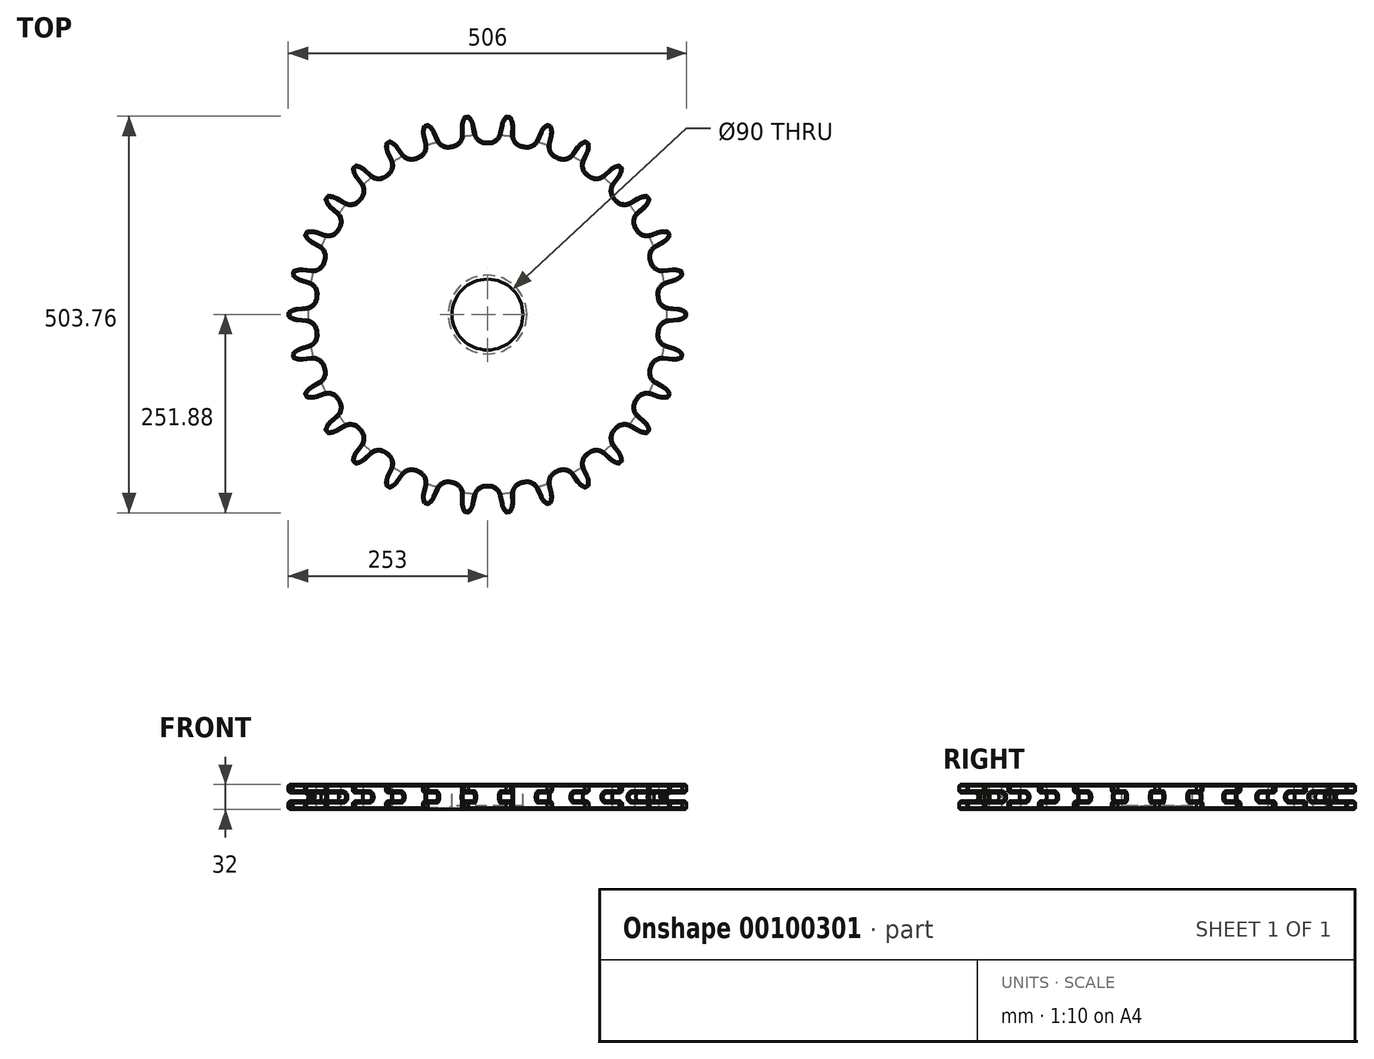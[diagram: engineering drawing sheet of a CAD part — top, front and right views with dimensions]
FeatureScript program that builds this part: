
annotation { "Feature Type Name" : "Feature", "Feature Type Description" : "" }
export const myFeature = defineFeature(function(context is Context, id is Id, definition is map)
    precondition{}
    {
        {
            var Q0;
            Q0=qCreatedBy(makeId("Top.planeOp"),FACE);
            var sketch = newSketch(context, id + "F0", { "sketchPlane" : qUnion([Q0])});
            skCircle(sketch, "E0", {"center": v(0, 0) * mm, "radius": 253 * mm});
            skCircle(sketch, "E1", {"center": v(0, 0) * mm, "radius": 216.9 * mm, "construction": true});
            skLineSegment(sketch, "E2", {"start": v(0, 0) * mm, "end": v(253, 0) * mm, "construction": true});
            skLineSegment(sketch, "E3", {"start": v(0, 0) * mm, "end": v(252.65, -13.34) * mm, "construction": true});
            skCircle(sketch, "E4", {"center": v(0, 0) * mm, "radius": 239.77 * mm, "construction": true});
            skCircle(sketch, "E5", {"center": v(239.43, -12.64) * mm, "radius": 20.44 * mm});
            skLineSegment(sketch, "E6", {"start": v(0, 0) * mm, "end": v(251.8, 24.61) * mm, "construction": true});
            skCircle(sketch, "E7", {"center": v(0, 0) * mm, "radius": 232.9 * mm, "construction": true});
            skCircle(sketch, "E8", {"center": v(231.8, 22.66) * mm, "radius": 14 * mm});
            skLineSegment(sketch, "E9", {"start": v(230.5, 8.72) * mm, "end": v(241.32, 7.72) * mm});
            skCircle(sketch, "E10", {"center": v(0, 0) * mm, "radius": 218.9 * mm});
            skSolve(sketch);
        }
        {
            var Q0;
            Q0=qCreatedBy(makeId("Top.planeOp"),FACE);
            var sketch = newSketch(context, id + "F1", { "sketchPlane" : qUnion([Q0])});
            skArc(sketch, "E11.0", {"start": v(217.86, 21.3) * mm, "mid": v(221.92, 12.73) * mm, "end": v(230.5, 8.72) * mm});
            skArc(sketch, "E12.0", {"start": v(252.99, 2.67) * mm, "mid": v(247.56, 6.12) * mm, "end": v(241.32, 7.72) * mm});
            skArc(sketch, "E13.0", {"start": v(253, 0) * mm, "mid": v(253, 1.33) * mm, "end": v(252.99, 2.67) * mm});
            skLineSegment(sketch, "E14.0", {"start": v(0, 0) * mm, "end": v(253, 0) * mm, "construction": true});
            skLineSegment(sketch, "E15.0", {"start": v(230.5, 8.72) * mm, "end": v(241.32, 7.72) * mm});
            skArc(sketch, "E16.MirrorCS", {"start": v(253, 0) * mm, "mid": v(253, -1.33) * mm, "end": v(252.99, -2.67) * mm});
            skArc(sketch, "E17.MirrorCS", {"start": v(252.99, -2.67) * mm, "mid": v(247.56, -6.12) * mm, "end": v(241.32, -7.72) * mm});
            skLineSegment(sketch, "E18.MirrorCS", {"start": v(230.5, -8.72) * mm, "end": v(241.32, -7.72) * mm});
            skArc(sketch, "E19.MirrorCS", {"start": v(217.86, -21.3) * mm, "mid": v(221.92, -12.73) * mm, "end": v(230.5, -8.72) * mm});
            skLineSegment(sketch, "E20.1.0", {"start": v(0, 0) * mm, "end": v(247.47, 52.6) * mm, "construction": true});
            skArc(sketch, "E20.1.1", {"start": v(208.68, 66.13) * mm, "mid": v(214.43, 58.6) * mm, "end": v(223.66, 56.45) * mm});
            skLineSegment(sketch, "E20.1.2", {"start": v(223.66, 56.45) * mm, "end": v(234.44, 57.72) * mm});
            skArc(sketch, "E20.1.3", {"start": v(246.9, 55.2) * mm, "mid": v(240.87, 57.46) * mm, "end": v(234.44, 57.72) * mm});
            skArc(sketch, "E20.1.4", {"start": v(247.47, 52.6) * mm, "mid": v(247.2, 53.9) * mm, "end": v(246.9, 55.2) * mm});
            skArc(sketch, "E20.1.5", {"start": v(247.47, 52.6) * mm, "mid": v(247.75, 51.3) * mm, "end": v(248.01, 50) * mm});
            skArc(sketch, "E20.1.6", {"start": v(248.01, 50) * mm, "mid": v(243.42, 45.48) * mm, "end": v(237.65, 42.63) * mm});
            skLineSegment(sketch, "E20.1.7", {"start": v(227.28, 39.4) * mm, "end": v(237.65, 42.63) * mm});
            skArc(sketch, "E20.1.8", {"start": v(217.53, 24.47) * mm, "mid": v(219.72, 33.68) * mm, "end": v(227.28, 39.4) * mm});
            skLineSegment(sketch, "E20.2.0", {"start": v(0, 0) * mm, "end": v(231.13, 102.9) * mm, "construction": true});
            skArc(sketch, "E20.2.1", {"start": v(190.37, 108.07) * mm, "mid": v(197.56, 101.9) * mm, "end": v(207.03, 101.72) * mm});
            skLineSegment(sketch, "E20.2.2", {"start": v(207.03, 101.72) * mm, "end": v(217.32, 105.2) * mm});
            skArc(sketch, "E20.2.3", {"start": v(230.03, 105.33) * mm, "mid": v(223.66, 106.28) * mm, "end": v(217.32, 105.2) * mm});
            skArc(sketch, "E20.2.4", {"start": v(231.13, 102.9) * mm, "mid": v(230.58, 104.12) * mm, "end": v(230.03, 105.33) * mm});
            skArc(sketch, "E20.2.5", {"start": v(231.13, 102.9) * mm, "mid": v(231.67, 101.69) * mm, "end": v(232.2, 100.46) * mm});
            skArc(sketch, "E20.2.6", {"start": v(232.2, 100.46) * mm, "mid": v(228.64, 95.1) * mm, "end": v(223.6, 91.1) * mm});
            skLineSegment(sketch, "E20.2.7", {"start": v(214.12, 85.8) * mm, "end": v(223.6, 91.1) * mm});
            skArc(sketch, "E20.2.8", {"start": v(207.7, 69.16) * mm, "mid": v(207.92, 78.63) * mm, "end": v(214.12, 85.8) * mm});
            skLineSegment(sketch, "E21.1.3.0", {"start": v(0, 0) * mm, "end": v(204.68, 148.7) * mm, "construction": true});
            skArc(sketch, "E21.3.3.0", {"start": v(163.74, 145.29) * mm, "mid": v(172.06, 140.75) * mm, "end": v(181.36, 142.54) * mm});
            skLineSegment(sketch, "E21.7.3.0", {"start": v(181.36, 142.54) * mm, "end": v(190.7, 148.09) * mm});
            skArc(sketch, "E21.10.3.0", {"start": v(203.1, 150.86) * mm, "mid": v(196.68, 150.46) * mm, "end": v(190.7, 148.09) * mm});
            skArc(sketch, "E21.14.3.0", {"start": v(204.68, 148.7) * mm, "mid": v(203.9, 149.79) * mm, "end": v(203.1, 150.86) * mm});
            skArc(sketch, "E21.18.3.0", {"start": v(204.68, 148.7) * mm, "mid": v(205.46, 147.63) * mm, "end": v(206.24, 146.54) * mm});
            skArc(sketch, "E21.22.3.0", {"start": v(206.24, 146.54) * mm, "mid": v(203.87, 140.56) * mm, "end": v(199.77, 135.6) * mm});
            skLineSegment(sketch, "E21.26.3.0", {"start": v(191.6, 128.44) * mm, "end": v(199.77, 135.6) * mm});
            skArc(sketch, "E21.29.3.0", {"start": v(188.77, 110.83) * mm, "mid": v(187.02, 120.14) * mm, "end": v(191.6, 128.44) * mm});
            skLineSegment(sketch, "E21.1.4.0", {"start": v(0, 0) * mm, "end": v(169.3, 188.02) * mm, "construction": true});
            skArc(sketch, "E21.3.4.0", {"start": v(129.95, 176.16) * mm, "mid": v(139.03, 173.44) * mm, "end": v(147.76, 177.13) * mm});
            skLineSegment(sketch, "E21.7.4.0", {"start": v(147.76, 177.13) * mm, "end": v(155.74, 184.5) * mm});
            skArc(sketch, "E21.10.4.0", {"start": v(167.3, 189.79) * mm, "mid": v(161.1, 188.07) * mm, "end": v(155.74, 184.5) * mm});
            skArc(sketch, "E21.14.4.0", {"start": v(169.3, 188.02) * mm, "mid": v(168.3, 188.9) * mm, "end": v(167.3, 189.79) * mm});
            skArc(sketch, "E21.18.4.0", {"start": v(169.3, 188.02) * mm, "mid": v(170.28, 187.12) * mm, "end": v(171.26, 186.22) * mm});
            skArc(sketch, "E21.22.4.0", {"start": v(171.26, 186.22) * mm, "mid": v(170.2, 179.87) * mm, "end": v(167.2, 174.17) * mm});
            skLineSegment(sketch, "E21.26.4.0", {"start": v(160.72, 165.47) * mm, "end": v(167.2, 174.17) * mm});
            skArc(sketch, "E21.29.4.0", {"start": v(161.6, 147.65) * mm, "mid": v(157.96, 156.4) * mm, "end": v(160.72, 165.47) * mm});
            skLineSegment(sketch, "E21.1.5.0", {"start": v(0, 0) * mm, "end": v(126.5, 219.1) * mm, "construction": true});
            skArc(sketch, "E21.3.5.0", {"start": v(90.49, 199.32) * mm, "mid": v(99.93, 198.56) * mm, "end": v(107.7, 203.98) * mm});
            skLineSegment(sketch, "E21.7.5.0", {"start": v(107.7, 203.98) * mm, "end": v(113.98, 212.85) * mm});
            skArc(sketch, "E21.10.5.0", {"start": v(124.18, 220.43) * mm, "mid": v(118.48, 217.45) * mm, "end": v(113.98, 212.85) * mm});
            skArc(sketch, "E21.14.5.0", {"start": v(126.5, 219.1) * mm, "mid": v(125.34, 219.77) * mm, "end": v(124.18, 220.43) * mm});
            skArc(sketch, "E21.18.5.0", {"start": v(126.5, 219.1) * mm, "mid": v(127.65, 218.43) * mm, "end": v(128.8, 217.76) * mm});
            skArc(sketch, "E21.22.5.0", {"start": v(128.8, 217.76) * mm, "mid": v(129.08, 211.33) * mm, "end": v(127.34, 205.13) * mm});
            skLineSegment(sketch, "E21.26.5.0", {"start": v(122.8, 195.27) * mm, "end": v(127.34, 205.13) * mm});
            skArc(sketch, "E21.29.5.0", {"start": v(127.38, 178.03) * mm, "mid": v(121.99, 185.82) * mm, "end": v(122.8, 195.27) * mm});
            skLineSegment(sketch, "E22.1.6.0", {"start": v(0, 0) * mm, "end": v(78.18, 240.62) * mm, "construction": true});
            skArc(sketch, "E22.3.6.0", {"start": v(47.07, 213.78) * mm, "mid": v(56.47, 215) * mm, "end": v(62.94, 221.92) * mm});
            skLineSegment(sketch, "E22.7.6.0", {"start": v(62.94, 221.92) * mm, "end": v(67.23, 231.9) * mm});
            skArc(sketch, "E22.10.6.0", {"start": v(75.64, 241.43) * mm, "mid": v(70.68, 237.33) * mm, "end": v(67.23, 231.9) * mm});
            skArc(sketch, "E22.14.6.0", {"start": v(78.18, 240.62) * mm, "mid": v(76.91, 241.03) * mm, "end": v(75.64, 241.43) * mm});
            skArc(sketch, "E22.18.6.0", {"start": v(78.18, 240.62) * mm, "mid": v(79.45, 240.2) * mm, "end": v(80.71, 239.78) * mm});
            skArc(sketch, "E22.22.6.0", {"start": v(80.71, 239.78) * mm, "mid": v(82.32, 233.55) * mm, "end": v(81.91, 227.12) * mm});
            skLineSegment(sketch, "E22.26.6.0", {"start": v(79.52, 216.53) * mm, "end": v(81.91, 227.12) * mm});
            skArc(sketch, "E22.29.6.0", {"start": v(87.58, 200.62) * mm, "mid": v(80.69, 207.13) * mm, "end": v(79.52, 216.53) * mm});
            skLineSegment(sketch, "E22.1.7.0", {"start": v(0, 0) * mm, "end": v(26.45, 251.61) * mm, "construction": true});
            skArc(sketch, "E22.3.7.0", {"start": v(1.6, 218.9) * mm, "mid": v(10.53, 222.04) * mm, "end": v(15.42, 230.16) * mm});
            skLineSegment(sketch, "E22.7.7.0", {"start": v(15.42, 230.16) * mm, "end": v(17.55, 240.8) * mm});
            skArc(sketch, "E22.10.7.0", {"start": v(23.8, 251.88) * mm, "mid": v(19.79, 246.84) * mm, "end": v(17.55, 240.8) * mm});
            skArc(sketch, "E22.14.7.0", {"start": v(26.45, 251.61) * mm, "mid": v(25.12, 251.75) * mm, "end": v(23.8, 251.88) * mm});
            skArc(sketch, "E22.18.7.0", {"start": v(26.45, 251.61) * mm, "mid": v(27.77, 251.47) * mm, "end": v(29.1, 251.32) * mm});
            skArc(sketch, "E22.22.7.0", {"start": v(29.1, 251.32) * mm, "mid": v(31.96, 245.56) * mm, "end": v(32.9, 239.2) * mm});
            skLineSegment(sketch, "E22.26.7.0", {"start": v(32.77, 228.33) * mm, "end": v(32.9, 239.2) * mm});
            skArc(sketch, "E22.29.7.0", {"start": v(43.95, 214.45) * mm, "mid": v(35.86, 219.38) * mm, "end": v(32.77, 228.33) * mm});
            skLineSegment(sketch, "E22.1.8.0", {"start": v(0, 0) * mm, "end": v(-26.45, 251.61) * mm, "construction": true});
            skArc(sketch, "E22.3.8.0", {"start": v(-43.95, 214.45) * mm, "mid": v(-35.86, 219.38) * mm, "end": v(-32.77, 228.33) * mm});
            skLineSegment(sketch, "E22.7.8.0", {"start": v(-32.77, 228.33) * mm, "end": v(-32.9, 239.2) * mm});
            skArc(sketch, "E22.10.8.0", {"start": v(-29.1, 251.32) * mm, "mid": v(-31.96, 245.56) * mm, "end": v(-32.9, 239.2) * mm});
            skArc(sketch, "E22.14.8.0", {"start": v(-26.45, 251.61) * mm, "mid": v(-27.77, 251.47) * mm, "end": v(-29.1, 251.32) * mm});
            skArc(sketch, "E22.18.8.0", {"start": v(-26.45, 251.61) * mm, "mid": v(-25.12, 251.75) * mm, "end": v(-23.8, 251.88) * mm});
            skArc(sketch, "E22.22.8.0", {"start": v(-23.8, 251.88) * mm, "mid": v(-19.79, 246.84) * mm, "end": v(-17.55, 240.8) * mm});
            skLineSegment(sketch, "E22.26.8.0", {"start": v(-15.42, 230.16) * mm, "end": v(-17.55, 240.8) * mm});
            skArc(sketch, "E22.29.8.0", {"start": v(-1.6, 218.9) * mm, "mid": v(-10.53, 222.04) * mm, "end": v(-15.42, 230.16) * mm});
            skLineSegment(sketch, "E22.1.9.0", {"start": v(0, 0) * mm, "end": v(-78.18, 240.62) * mm, "construction": true});
            skArc(sketch, "E22.3.9.0", {"start": v(-87.58, 200.62) * mm, "mid": v(-80.69, 207.13) * mm, "end": v(-79.52, 216.53) * mm});
            skLineSegment(sketch, "E22.7.9.0", {"start": v(-79.52, 216.53) * mm, "end": v(-81.91, 227.12) * mm});
            skArc(sketch, "E22.10.9.0", {"start": v(-80.71, 239.78) * mm, "mid": v(-82.32, 233.55) * mm, "end": v(-81.91, 227.12) * mm});
            skArc(sketch, "E22.14.9.0", {"start": v(-78.18, 240.62) * mm, "mid": v(-79.45, 240.2) * mm, "end": v(-80.71, 239.78) * mm});
            skArc(sketch, "E22.18.9.0", {"start": v(-78.18, 240.62) * mm, "mid": v(-76.91, 241.03) * mm, "end": v(-75.64, 241.43) * mm});
            skArc(sketch, "E22.22.9.0", {"start": v(-75.64, 241.43) * mm, "mid": v(-70.68, 237.33) * mm, "end": v(-67.23, 231.9) * mm});
            skLineSegment(sketch, "E22.26.9.0", {"start": v(-62.94, 221.92) * mm, "end": v(-67.23, 231.9) * mm});
            skArc(sketch, "E22.29.9.0", {"start": v(-47.07, 213.78) * mm, "mid": v(-56.47, 215) * mm, "end": v(-62.94, 221.92) * mm});
            skLineSegment(sketch, "E22.1.10.0", {"start": v(0, 0) * mm, "end": v(-126.5, 219.1) * mm, "construction": true});
            skArc(sketch, "E22.3.10.0", {"start": v(-127.38, 178.03) * mm, "mid": v(-121.99, 185.82) * mm, "end": v(-122.8, 195.27) * mm});
            skLineSegment(sketch, "E22.7.10.0", {"start": v(-122.8, 195.27) * mm, "end": v(-127.34, 205.13) * mm});
            skArc(sketch, "E22.10.10.0", {"start": v(-128.8, 217.76) * mm, "mid": v(-129.08, 211.33) * mm, "end": v(-127.34, 205.13) * mm});
            skArc(sketch, "E22.14.10.0", {"start": v(-126.5, 219.1) * mm, "mid": v(-127.65, 218.43) * mm, "end": v(-128.8, 217.76) * mm});
            skArc(sketch, "E22.18.10.0", {"start": v(-126.5, 219.1) * mm, "mid": v(-125.34, 219.77) * mm, "end": v(-124.18, 220.43) * mm});
            skArc(sketch, "E22.22.10.0", {"start": v(-124.18, 220.43) * mm, "mid": v(-118.48, 217.45) * mm, "end": v(-113.98, 212.85) * mm});
            skLineSegment(sketch, "E22.26.10.0", {"start": v(-107.7, 203.98) * mm, "end": v(-113.98, 212.85) * mm});
            skArc(sketch, "E22.29.10.0", {"start": v(-90.49, 199.32) * mm, "mid": v(-99.93, 198.56) * mm, "end": v(-107.7, 203.98) * mm});
            skLineSegment(sketch, "E22.1.11.0", {"start": v(0, 0) * mm, "end": v(-169.3, 188.02) * mm, "construction": true});
            skArc(sketch, "E22.3.11.0", {"start": v(-161.6, 147.65) * mm, "mid": v(-157.96, 156.4) * mm, "end": v(-160.72, 165.47) * mm});
            skLineSegment(sketch, "E22.7.11.0", {"start": v(-160.72, 165.47) * mm, "end": v(-167.2, 174.17) * mm});
            skArc(sketch, "E22.10.11.0", {"start": v(-171.26, 186.22) * mm, "mid": v(-170.2, 179.87) * mm, "end": v(-167.2, 174.17) * mm});
            skArc(sketch, "E22.14.11.0", {"start": v(-169.3, 188.02) * mm, "mid": v(-170.28, 187.12) * mm, "end": v(-171.26, 186.22) * mm});
            skArc(sketch, "E22.18.11.0", {"start": v(-169.3, 188.02) * mm, "mid": v(-168.3, 188.9) * mm, "end": v(-167.3, 189.79) * mm});
            skArc(sketch, "E22.22.11.0", {"start": v(-167.3, 189.79) * mm, "mid": v(-161.1, 188.07) * mm, "end": v(-155.74, 184.5) * mm});
            skLineSegment(sketch, "E22.26.11.0", {"start": v(-147.76, 177.13) * mm, "end": v(-155.74, 184.5) * mm});
            skArc(sketch, "E22.29.11.0", {"start": v(-129.95, 176.16) * mm, "mid": v(-139.03, 173.44) * mm, "end": v(-147.76, 177.13) * mm});
            skLineSegment(sketch, "E22.1.12.0", {"start": v(0, 0) * mm, "end": v(-204.68, 148.7) * mm, "construction": true});
            skArc(sketch, "E22.3.12.0", {"start": v(-188.77, 110.83) * mm, "mid": v(-187.02, 120.14) * mm, "end": v(-191.6, 128.44) * mm});
            skLineSegment(sketch, "E22.7.12.0", {"start": v(-191.6, 128.44) * mm, "end": v(-199.77, 135.6) * mm});
            skArc(sketch, "E22.10.12.0", {"start": v(-206.24, 146.54) * mm, "mid": v(-203.87, 140.56) * mm, "end": v(-199.77, 135.6) * mm});
            skArc(sketch, "E22.14.12.0", {"start": v(-204.68, 148.7) * mm, "mid": v(-205.46, 147.63) * mm, "end": v(-206.24, 146.54) * mm});
            skArc(sketch, "E22.18.12.0", {"start": v(-204.68, 148.7) * mm, "mid": v(-203.9, 149.79) * mm, "end": v(-203.1, 150.86) * mm});
            skArc(sketch, "E22.22.12.0", {"start": v(-203.1, 150.86) * mm, "mid": v(-196.68, 150.46) * mm, "end": v(-190.7, 148.09) * mm});
            skLineSegment(sketch, "E22.26.12.0", {"start": v(-181.36, 142.54) * mm, "end": v(-190.7, 148.09) * mm});
            skArc(sketch, "E22.29.12.0", {"start": v(-163.74, 145.29) * mm, "mid": v(-172.06, 140.75) * mm, "end": v(-181.36, 142.54) * mm});
            skLineSegment(sketch, "E22.1.13.0", {"start": v(0, 0) * mm, "end": v(-231.13, 102.9) * mm, "construction": true});
            skArc(sketch, "E22.3.13.0", {"start": v(-207.7, 69.16) * mm, "mid": v(-207.92, 78.63) * mm, "end": v(-214.12, 85.8) * mm});
            skLineSegment(sketch, "E22.7.13.0", {"start": v(-214.12, 85.8) * mm, "end": v(-223.6, 91.1) * mm});
            skArc(sketch, "E22.10.13.0", {"start": v(-232.2, 100.46) * mm, "mid": v(-228.64, 95.1) * mm, "end": v(-223.6, 91.1) * mm});
            skArc(sketch, "E22.14.13.0", {"start": v(-231.13, 102.9) * mm, "mid": v(-231.67, 101.69) * mm, "end": v(-232.2, 100.46) * mm});
            skArc(sketch, "E22.18.13.0", {"start": v(-231.13, 102.9) * mm, "mid": v(-230.58, 104.12) * mm, "end": v(-230.03, 105.33) * mm});
            skArc(sketch, "E22.22.13.0", {"start": v(-230.03, 105.33) * mm, "mid": v(-223.66, 106.28) * mm, "end": v(-217.32, 105.2) * mm});
            skLineSegment(sketch, "E22.26.13.0", {"start": v(-207.03, 101.72) * mm, "end": v(-217.32, 105.2) * mm});
            skArc(sketch, "E22.29.13.0", {"start": v(-190.37, 108.07) * mm, "mid": v(-197.56, 101.9) * mm, "end": v(-207.03, 101.72) * mm});
            skLineSegment(sketch, "E22.1.14.0", {"start": v(0, 0) * mm, "end": v(-247.47, 52.6) * mm, "construction": true});
            skArc(sketch, "E22.3.14.0", {"start": v(-217.53, 24.47) * mm, "mid": v(-219.72, 33.68) * mm, "end": v(-227.28, 39.4) * mm});
            skLineSegment(sketch, "E22.7.14.0", {"start": v(-227.28, 39.4) * mm, "end": v(-237.65, 42.63) * mm});
            skArc(sketch, "E22.10.14.0", {"start": v(-248.01, 50) * mm, "mid": v(-243.42, 45.48) * mm, "end": v(-237.65, 42.63) * mm});
            skArc(sketch, "E22.14.14.0", {"start": v(-247.47, 52.6) * mm, "mid": v(-247.75, 51.3) * mm, "end": v(-248.01, 50) * mm});
            skArc(sketch, "E22.18.14.0", {"start": v(-247.47, 52.6) * mm, "mid": v(-247.2, 53.9) * mm, "end": v(-246.9, 55.2) * mm});
            skArc(sketch, "E22.22.14.0", {"start": v(-246.9, 55.2) * mm, "mid": v(-240.87, 57.46) * mm, "end": v(-234.44, 57.72) * mm});
            skLineSegment(sketch, "E22.26.14.0", {"start": v(-223.66, 56.45) * mm, "end": v(-234.44, 57.72) * mm});
            skArc(sketch, "E22.29.14.0", {"start": v(-208.68, 66.13) * mm, "mid": v(-214.43, 58.6) * mm, "end": v(-223.66, 56.45) * mm});
            skLineSegment(sketch, "E22.1.15.0", {"start": v(0, 0) * mm, "end": v(-253, 0) * mm, "construction": true});
            skArc(sketch, "E22.3.15.0", {"start": v(-217.86, -21.3) * mm, "mid": v(-221.92, -12.73) * mm, "end": v(-230.5, -8.72) * mm});
            skLineSegment(sketch, "E22.7.15.0", {"start": v(-230.5, -8.72) * mm, "end": v(-241.32, -7.72) * mm});
            skArc(sketch, "E22.10.15.0", {"start": v(-252.99, -2.67) * mm, "mid": v(-247.56, -6.12) * mm, "end": v(-241.32, -7.72) * mm});
            skArc(sketch, "E22.14.15.0", {"start": v(-253, 0) * mm, "mid": v(-253, -1.33) * mm, "end": v(-252.99, -2.67) * mm});
            skArc(sketch, "E22.18.15.0", {"start": v(-253, 0) * mm, "mid": v(-253, 1.33) * mm, "end": v(-252.99, 2.67) * mm});
            skArc(sketch, "E22.22.15.0", {"start": v(-252.99, 2.67) * mm, "mid": v(-247.56, 6.12) * mm, "end": v(-241.32, 7.72) * mm});
            skLineSegment(sketch, "E22.26.15.0", {"start": v(-230.5, 8.72) * mm, "end": v(-241.32, 7.72) * mm});
            skArc(sketch, "E22.29.15.0", {"start": v(-217.86, 21.3) * mm, "mid": v(-221.92, 12.73) * mm, "end": v(-230.5, 8.72) * mm});
            skLineSegment(sketch, "E22.1.16.0", {"start": v(0, 0) * mm, "end": v(-247.47, -52.6) * mm, "construction": true});
            skArc(sketch, "E22.3.16.0", {"start": v(-208.68, -66.13) * mm, "mid": v(-214.43, -58.6) * mm, "end": v(-223.66, -56.45) * mm});
            skLineSegment(sketch, "E22.7.16.0", {"start": v(-223.66, -56.45) * mm, "end": v(-234.44, -57.72) * mm});
            skArc(sketch, "E22.10.16.0", {"start": v(-246.9, -55.2) * mm, "mid": v(-240.87, -57.46) * mm, "end": v(-234.44, -57.72) * mm});
            skArc(sketch, "E22.14.16.0", {"start": v(-247.47, -52.6) * mm, "mid": v(-247.2, -53.9) * mm, "end": v(-246.9, -55.2) * mm});
            skArc(sketch, "E22.18.16.0", {"start": v(-247.47, -52.6) * mm, "mid": v(-247.75, -51.3) * mm, "end": v(-248.01, -50) * mm});
            skArc(sketch, "E22.22.16.0", {"start": v(-248.01, -50) * mm, "mid": v(-243.42, -45.48) * mm, "end": v(-237.65, -42.63) * mm});
            skLineSegment(sketch, "E22.26.16.0", {"start": v(-227.28, -39.4) * mm, "end": v(-237.65, -42.63) * mm});
            skArc(sketch, "E22.29.16.0", {"start": v(-217.53, -24.47) * mm, "mid": v(-219.72, -33.68) * mm, "end": v(-227.28, -39.4) * mm});
            skLineSegment(sketch, "E22.1.17.0", {"start": v(0, 0) * mm, "end": v(-231.13, -102.9) * mm, "construction": true});
            skArc(sketch, "E22.3.17.0", {"start": v(-190.37, -108.07) * mm, "mid": v(-197.56, -101.9) * mm, "end": v(-207.03, -101.72) * mm});
            skLineSegment(sketch, "E22.7.17.0", {"start": v(-207.03, -101.72) * mm, "end": v(-217.32, -105.2) * mm});
            skArc(sketch, "E22.10.17.0", {"start": v(-230.03, -105.33) * mm, "mid": v(-223.66, -106.28) * mm, "end": v(-217.32, -105.2) * mm});
            skArc(sketch, "E22.14.17.0", {"start": v(-231.13, -102.9) * mm, "mid": v(-230.58, -104.12) * mm, "end": v(-230.03, -105.33) * mm});
            skArc(sketch, "E22.18.17.0", {"start": v(-231.13, -102.9) * mm, "mid": v(-231.67, -101.69) * mm, "end": v(-232.2, -100.46) * mm});
            skArc(sketch, "E22.22.17.0", {"start": v(-232.2, -100.46) * mm, "mid": v(-228.64, -95.1) * mm, "end": v(-223.6, -91.1) * mm});
            skLineSegment(sketch, "E22.26.17.0", {"start": v(-214.12, -85.8) * mm, "end": v(-223.6, -91.1) * mm});
            skArc(sketch, "E22.29.17.0", {"start": v(-207.7, -69.16) * mm, "mid": v(-207.92, -78.63) * mm, "end": v(-214.12, -85.8) * mm});
            skLineSegment(sketch, "E22.1.18.0", {"start": v(0, 0) * mm, "end": v(-204.68, -148.7) * mm, "construction": true});
            skArc(sketch, "E22.3.18.0", {"start": v(-163.74, -145.29) * mm, "mid": v(-172.06, -140.75) * mm, "end": v(-181.36, -142.54) * mm});
            skLineSegment(sketch, "E22.7.18.0", {"start": v(-181.36, -142.54) * mm, "end": v(-190.7, -148.09) * mm});
            skArc(sketch, "E22.10.18.0", {"start": v(-203.1, -150.86) * mm, "mid": v(-196.68, -150.46) * mm, "end": v(-190.7, -148.09) * mm});
            skArc(sketch, "E22.14.18.0", {"start": v(-204.68, -148.7) * mm, "mid": v(-203.9, -149.79) * mm, "end": v(-203.1, -150.86) * mm});
            skArc(sketch, "E22.18.18.0", {"start": v(-204.68, -148.7) * mm, "mid": v(-205.46, -147.63) * mm, "end": v(-206.24, -146.54) * mm});
            skArc(sketch, "E22.22.18.0", {"start": v(-206.24, -146.54) * mm, "mid": v(-203.87, -140.56) * mm, "end": v(-199.77, -135.6) * mm});
            skLineSegment(sketch, "E22.26.18.0", {"start": v(-191.6, -128.44) * mm, "end": v(-199.77, -135.6) * mm});
            skArc(sketch, "E22.29.18.0", {"start": v(-188.77, -110.83) * mm, "mid": v(-187.02, -120.14) * mm, "end": v(-191.6, -128.44) * mm});
            skLineSegment(sketch, "E22.1.19.0", {"start": v(0, 0) * mm, "end": v(-169.3, -188.02) * mm, "construction": true});
            skArc(sketch, "E22.3.19.0", {"start": v(-129.95, -176.16) * mm, "mid": v(-139.03, -173.44) * mm, "end": v(-147.76, -177.13) * mm});
            skLineSegment(sketch, "E22.7.19.0", {"start": v(-147.76, -177.13) * mm, "end": v(-155.74, -184.5) * mm});
            skArc(sketch, "E22.10.19.0", {"start": v(-167.3, -189.79) * mm, "mid": v(-161.1, -188.07) * mm, "end": v(-155.74, -184.5) * mm});
            skArc(sketch, "E22.14.19.0", {"start": v(-169.3, -188.02) * mm, "mid": v(-168.3, -188.9) * mm, "end": v(-167.3, -189.79) * mm});
            skArc(sketch, "E22.18.19.0", {"start": v(-169.3, -188.02) * mm, "mid": v(-170.28, -187.12) * mm, "end": v(-171.26, -186.22) * mm});
            skArc(sketch, "E22.22.19.0", {"start": v(-171.26, -186.22) * mm, "mid": v(-170.2, -179.87) * mm, "end": v(-167.2, -174.17) * mm});
            skLineSegment(sketch, "E22.26.19.0", {"start": v(-160.72, -165.47) * mm, "end": v(-167.2, -174.17) * mm});
            skArc(sketch, "E22.29.19.0", {"start": v(-161.6, -147.65) * mm, "mid": v(-157.96, -156.4) * mm, "end": v(-160.72, -165.47) * mm});
            skLineSegment(sketch, "E22.1.20.0", {"start": v(0, 0) * mm, "end": v(-126.5, -219.1) * mm, "construction": true});
            skArc(sketch, "E22.3.20.0", {"start": v(-90.49, -199.32) * mm, "mid": v(-99.93, -198.56) * mm, "end": v(-107.7, -203.98) * mm});
            skLineSegment(sketch, "E22.7.20.0", {"start": v(-107.7, -203.98) * mm, "end": v(-113.98, -212.85) * mm});
            skArc(sketch, "E22.10.20.0", {"start": v(-124.18, -220.43) * mm, "mid": v(-118.48, -217.45) * mm, "end": v(-113.98, -212.85) * mm});
            skArc(sketch, "E22.14.20.0", {"start": v(-126.5, -219.1) * mm, "mid": v(-125.34, -219.77) * mm, "end": v(-124.18, -220.43) * mm});
            skArc(sketch, "E22.18.20.0", {"start": v(-126.5, -219.1) * mm, "mid": v(-127.65, -218.43) * mm, "end": v(-128.8, -217.76) * mm});
            skArc(sketch, "E22.22.20.0", {"start": v(-128.8, -217.76) * mm, "mid": v(-129.08, -211.33) * mm, "end": v(-127.34, -205.13) * mm});
            skLineSegment(sketch, "E22.26.20.0", {"start": v(-122.8, -195.27) * mm, "end": v(-127.34, -205.13) * mm});
            skArc(sketch, "E22.29.20.0", {"start": v(-127.38, -178.03) * mm, "mid": v(-121.99, -185.82) * mm, "end": v(-122.8, -195.27) * mm});
            skLineSegment(sketch, "E22.1.21.0", {"start": v(0, 0) * mm, "end": v(-78.18, -240.62) * mm, "construction": true});
            skArc(sketch, "E22.3.21.0", {"start": v(-47.07, -213.78) * mm, "mid": v(-56.47, -215) * mm, "end": v(-62.94, -221.92) * mm});
            skLineSegment(sketch, "E22.7.21.0", {"start": v(-62.94, -221.92) * mm, "end": v(-67.23, -231.9) * mm});
            skArc(sketch, "E22.10.21.0", {"start": v(-75.64, -241.43) * mm, "mid": v(-70.68, -237.33) * mm, "end": v(-67.23, -231.9) * mm});
            skArc(sketch, "E22.14.21.0", {"start": v(-78.18, -240.62) * mm, "mid": v(-76.91, -241.03) * mm, "end": v(-75.64, -241.43) * mm});
            skArc(sketch, "E22.18.21.0", {"start": v(-78.18, -240.62) * mm, "mid": v(-79.45, -240.2) * mm, "end": v(-80.71, -239.78) * mm});
            skArc(sketch, "E22.22.21.0", {"start": v(-80.71, -239.78) * mm, "mid": v(-82.32, -233.55) * mm, "end": v(-81.91, -227.12) * mm});
            skLineSegment(sketch, "E22.26.21.0", {"start": v(-79.52, -216.53) * mm, "end": v(-81.91, -227.12) * mm});
            skArc(sketch, "E22.29.21.0", {"start": v(-87.58, -200.62) * mm, "mid": v(-80.69, -207.13) * mm, "end": v(-79.52, -216.53) * mm});
            skLineSegment(sketch, "E22.1.22.0", {"start": v(0, 0) * mm, "end": v(-26.45, -251.61) * mm, "construction": true});
            skArc(sketch, "E22.3.22.0", {"start": v(-1.6, -218.9) * mm, "mid": v(-10.53, -222.04) * mm, "end": v(-15.42, -230.16) * mm});
            skLineSegment(sketch, "E22.7.22.0", {"start": v(-15.42, -230.16) * mm, "end": v(-17.55, -240.8) * mm});
            skArc(sketch, "E22.10.22.0", {"start": v(-23.8, -251.88) * mm, "mid": v(-19.79, -246.84) * mm, "end": v(-17.55, -240.8) * mm});
            skArc(sketch, "E22.14.22.0", {"start": v(-26.45, -251.61) * mm, "mid": v(-25.12, -251.75) * mm, "end": v(-23.8, -251.88) * mm});
            skArc(sketch, "E22.18.22.0", {"start": v(-26.45, -251.61) * mm, "mid": v(-27.77, -251.47) * mm, "end": v(-29.1, -251.32) * mm});
            skArc(sketch, "E22.22.22.0", {"start": v(-29.1, -251.32) * mm, "mid": v(-31.96, -245.56) * mm, "end": v(-32.9, -239.2) * mm});
            skLineSegment(sketch, "E22.26.22.0", {"start": v(-32.77, -228.33) * mm, "end": v(-32.9, -239.2) * mm});
            skArc(sketch, "E22.29.22.0", {"start": v(-43.95, -214.45) * mm, "mid": v(-35.86, -219.38) * mm, "end": v(-32.77, -228.33) * mm});
            skLineSegment(sketch, "E22.1.23.0", {"start": v(0, 0) * mm, "end": v(26.45, -251.61) * mm, "construction": true});
            skArc(sketch, "E22.3.23.0", {"start": v(43.95, -214.45) * mm, "mid": v(35.86, -219.38) * mm, "end": v(32.77, -228.33) * mm});
            skLineSegment(sketch, "E22.7.23.0", {"start": v(32.77, -228.33) * mm, "end": v(32.9, -239.2) * mm});
            skArc(sketch, "E22.10.23.0", {"start": v(29.1, -251.32) * mm, "mid": v(31.96, -245.56) * mm, "end": v(32.9, -239.2) * mm});
            skArc(sketch, "E22.14.23.0", {"start": v(26.45, -251.61) * mm, "mid": v(27.77, -251.47) * mm, "end": v(29.1, -251.32) * mm});
            skArc(sketch, "E22.18.23.0", {"start": v(26.45, -251.61) * mm, "mid": v(25.12, -251.75) * mm, "end": v(23.8, -251.88) * mm});
            skArc(sketch, "E22.22.23.0", {"start": v(23.8, -251.88) * mm, "mid": v(19.79, -246.84) * mm, "end": v(17.55, -240.8) * mm});
            skLineSegment(sketch, "E22.26.23.0", {"start": v(15.42, -230.16) * mm, "end": v(17.55, -240.8) * mm});
            skArc(sketch, "E22.29.23.0", {"start": v(1.6, -218.9) * mm, "mid": v(10.53, -222.04) * mm, "end": v(15.42, -230.16) * mm});
            skLineSegment(sketch, "E22.1.24.0", {"start": v(0, 0) * mm, "end": v(78.18, -240.62) * mm, "construction": true});
            skArc(sketch, "E22.3.24.0", {"start": v(87.58, -200.62) * mm, "mid": v(80.69, -207.13) * mm, "end": v(79.52, -216.53) * mm});
            skLineSegment(sketch, "E22.7.24.0", {"start": v(79.52, -216.53) * mm, "end": v(81.91, -227.12) * mm});
            skArc(sketch, "E22.10.24.0", {"start": v(80.71, -239.78) * mm, "mid": v(82.32, -233.55) * mm, "end": v(81.91, -227.12) * mm});
            skArc(sketch, "E22.14.24.0", {"start": v(78.18, -240.62) * mm, "mid": v(79.45, -240.2) * mm, "end": v(80.71, -239.78) * mm});
            skArc(sketch, "E22.18.24.0", {"start": v(78.18, -240.62) * mm, "mid": v(76.91, -241.03) * mm, "end": v(75.64, -241.43) * mm});
            skArc(sketch, "E22.22.24.0", {"start": v(75.64, -241.43) * mm, "mid": v(70.68, -237.33) * mm, "end": v(67.23, -231.9) * mm});
            skLineSegment(sketch, "E22.26.24.0", {"start": v(62.94, -221.92) * mm, "end": v(67.23, -231.9) * mm});
            skArc(sketch, "E22.29.24.0", {"start": v(47.07, -213.78) * mm, "mid": v(56.47, -215) * mm, "end": v(62.94, -221.92) * mm});
            skLineSegment(sketch, "E22.1.25.0", {"start": v(0, 0) * mm, "end": v(126.5, -219.1) * mm, "construction": true});
            skArc(sketch, "E22.3.25.0", {"start": v(127.38, -178.03) * mm, "mid": v(121.99, -185.82) * mm, "end": v(122.8, -195.27) * mm});
            skLineSegment(sketch, "E22.7.25.0", {"start": v(122.8, -195.27) * mm, "end": v(127.34, -205.13) * mm});
            skArc(sketch, "E22.10.25.0", {"start": v(128.8, -217.76) * mm, "mid": v(129.08, -211.33) * mm, "end": v(127.34, -205.13) * mm});
            skArc(sketch, "E22.14.25.0", {"start": v(126.5, -219.1) * mm, "mid": v(127.65, -218.43) * mm, "end": v(128.8, -217.76) * mm});
            skArc(sketch, "E22.18.25.0", {"start": v(126.5, -219.1) * mm, "mid": v(125.34, -219.77) * mm, "end": v(124.18, -220.43) * mm});
            skArc(sketch, "E22.22.25.0", {"start": v(124.18, -220.43) * mm, "mid": v(118.48, -217.45) * mm, "end": v(113.98, -212.85) * mm});
            skLineSegment(sketch, "E22.26.25.0", {"start": v(107.7, -203.98) * mm, "end": v(113.98, -212.85) * mm});
            skArc(sketch, "E22.29.25.0", {"start": v(90.49, -199.32) * mm, "mid": v(99.93, -198.56) * mm, "end": v(107.7, -203.98) * mm});
            skLineSegment(sketch, "E22.1.26.0", {"start": v(0, 0) * mm, "end": v(169.3, -188.02) * mm, "construction": true});
            skArc(sketch, "E22.3.26.0", {"start": v(161.6, -147.65) * mm, "mid": v(157.96, -156.4) * mm, "end": v(160.72, -165.47) * mm});
            skLineSegment(sketch, "E22.7.26.0", {"start": v(160.72, -165.47) * mm, "end": v(167.2, -174.17) * mm});
            skArc(sketch, "E22.10.26.0", {"start": v(171.26, -186.22) * mm, "mid": v(170.2, -179.87) * mm, "end": v(167.2, -174.17) * mm});
            skArc(sketch, "E22.14.26.0", {"start": v(169.3, -188.02) * mm, "mid": v(170.28, -187.12) * mm, "end": v(171.26, -186.22) * mm});
            skArc(sketch, "E22.18.26.0", {"start": v(169.3, -188.02) * mm, "mid": v(168.3, -188.9) * mm, "end": v(167.3, -189.79) * mm});
            skArc(sketch, "E22.22.26.0", {"start": v(167.3, -189.79) * mm, "mid": v(161.1, -188.07) * mm, "end": v(155.74, -184.5) * mm});
            skLineSegment(sketch, "E22.26.26.0", {"start": v(147.76, -177.13) * mm, "end": v(155.74, -184.5) * mm});
            skArc(sketch, "E22.29.26.0", {"start": v(129.95, -176.16) * mm, "mid": v(139.03, -173.44) * mm, "end": v(147.76, -177.13) * mm});
            skLineSegment(sketch, "E22.1.27.0", {"start": v(0, 0) * mm, "end": v(204.68, -148.7) * mm, "construction": true});
            skArc(sketch, "E22.3.27.0", {"start": v(188.77, -110.83) * mm, "mid": v(187.02, -120.14) * mm, "end": v(191.6, -128.44) * mm});
            skLineSegment(sketch, "E22.7.27.0", {"start": v(191.6, -128.44) * mm, "end": v(199.77, -135.6) * mm});
            skArc(sketch, "E22.10.27.0", {"start": v(206.24, -146.54) * mm, "mid": v(203.87, -140.56) * mm, "end": v(199.77, -135.6) * mm});
            skArc(sketch, "E22.14.27.0", {"start": v(204.68, -148.7) * mm, "mid": v(205.46, -147.63) * mm, "end": v(206.24, -146.54) * mm});
            skArc(sketch, "E22.18.27.0", {"start": v(204.68, -148.7) * mm, "mid": v(203.9, -149.79) * mm, "end": v(203.1, -150.86) * mm});
            skArc(sketch, "E22.22.27.0", {"start": v(203.1, -150.86) * mm, "mid": v(196.68, -150.46) * mm, "end": v(190.7, -148.09) * mm});
            skLineSegment(sketch, "E22.26.27.0", {"start": v(181.36, -142.54) * mm, "end": v(190.7, -148.09) * mm});
            skArc(sketch, "E22.29.27.0", {"start": v(163.74, -145.29) * mm, "mid": v(172.06, -140.75) * mm, "end": v(181.36, -142.54) * mm});
            skLineSegment(sketch, "E22.1.28.0", {"start": v(0, 0) * mm, "end": v(231.13, -102.9) * mm, "construction": true});
            skArc(sketch, "E22.3.28.0", {"start": v(207.7, -69.16) * mm, "mid": v(207.92, -78.63) * mm, "end": v(214.12, -85.8) * mm});
            skLineSegment(sketch, "E22.7.28.0", {"start": v(214.12, -85.8) * mm, "end": v(223.6, -91.1) * mm});
            skArc(sketch, "E22.10.28.0", {"start": v(232.2, -100.46) * mm, "mid": v(228.64, -95.1) * mm, "end": v(223.6, -91.1) * mm});
            skArc(sketch, "E22.14.28.0", {"start": v(231.13, -102.9) * mm, "mid": v(231.67, -101.69) * mm, "end": v(232.2, -100.46) * mm});
            skArc(sketch, "E22.18.28.0", {"start": v(231.13, -102.9) * mm, "mid": v(230.58, -104.12) * mm, "end": v(230.03, -105.33) * mm});
            skArc(sketch, "E22.22.28.0", {"start": v(230.03, -105.33) * mm, "mid": v(223.66, -106.28) * mm, "end": v(217.32, -105.2) * mm});
            skLineSegment(sketch, "E22.26.28.0", {"start": v(207.03, -101.72) * mm, "end": v(217.32, -105.2) * mm});
            skArc(sketch, "E22.29.28.0", {"start": v(190.37, -108.07) * mm, "mid": v(197.56, -101.9) * mm, "end": v(207.03, -101.72) * mm});
            skLineSegment(sketch, "E22.1.29.0", {"start": v(0, 0) * mm, "end": v(247.47, -52.6) * mm, "construction": true});
            skArc(sketch, "E22.3.29.0", {"start": v(217.53, -24.47) * mm, "mid": v(219.72, -33.68) * mm, "end": v(227.28, -39.4) * mm});
            skLineSegment(sketch, "E22.7.29.0", {"start": v(227.28, -39.4) * mm, "end": v(237.65, -42.63) * mm});
            skArc(sketch, "E22.10.29.0", {"start": v(248.01, -50) * mm, "mid": v(243.42, -45.48) * mm, "end": v(237.65, -42.63) * mm});
            skArc(sketch, "E22.14.29.0", {"start": v(247.47, -52.6) * mm, "mid": v(247.75, -51.3) * mm, "end": v(248.01, -50) * mm});
            skArc(sketch, "E22.18.29.0", {"start": v(247.47, -52.6) * mm, "mid": v(247.2, -53.9) * mm, "end": v(246.9, -55.2) * mm});
            skArc(sketch, "E22.22.29.0", {"start": v(246.9, -55.2) * mm, "mid": v(240.87, -57.46) * mm, "end": v(234.44, -57.72) * mm});
            skLineSegment(sketch, "E22.26.29.0", {"start": v(223.66, -56.45) * mm, "end": v(234.44, -57.72) * mm});
            skArc(sketch, "E22.29.29.0", {"start": v(208.68, -66.13) * mm, "mid": v(214.43, -58.6) * mm, "end": v(223.66, -56.45) * mm});
            skArc(sketch, "E23", {"start": v(-217.86, -21.3) * mm, "mid": v(-217.7, -22.88) * mm, "end": v(-217.53, -24.47) * mm});
            skArc(sketch, "E24.trimOffspring", {"start": v(-208.68, -66.13) * mm, "mid": v(-208.19, -67.64) * mm, "end": v(-207.7, -69.16) * mm});
            skArc(sketch, "E25.trimOffspring", {"start": v(-217.53, 24.47) * mm, "mid": v(-217.7, 22.88) * mm, "end": v(-217.86, 21.3) * mm});
            skArc(sketch, "E26.trimOffspring", {"start": v(-207.7, 69.16) * mm, "mid": v(-208.19, 67.64) * mm, "end": v(-208.68, 66.13) * mm});
            skArc(sketch, "E27.trimOffspring", {"start": v(-188.77, 110.83) * mm, "mid": v(-189.58, 109.45) * mm, "end": v(-190.37, 108.07) * mm});
            skArc(sketch, "E28.trimOffspring", {"start": v(-161.6, 147.65) * mm, "mid": v(-162.68, 146.47) * mm, "end": v(-163.74, 145.29) * mm});
            skArc(sketch, "E29.trimOffspring", {"start": v(-127.38, 178.03) * mm, "mid": v(-128.67, 177.1) * mm, "end": v(-129.95, 176.16) * mm});
            skArc(sketch, "E30.trimOffspring", {"start": v(-87.58, 200.62) * mm, "mid": v(-89.04, 199.98) * mm, "end": v(-90.49, 199.32) * mm});
            skArc(sketch, "E31.trimOffspring", {"start": v(-43.95, 214.45) * mm, "mid": v(-45.51, 214.12) * mm, "end": v(-47.07, 213.78) * mm});
            skArc(sketch, "E32.trimOffspring", {"start": v(1.6, 218.9) * mm, "mid": v(0, 218.9) * mm, "end": v(-1.6, 218.9) * mm});
            skArc(sketch, "E33.trimOffspring", {"start": v(47.07, 213.78) * mm, "mid": v(45.51, 214.12) * mm, "end": v(43.95, 214.45) * mm});
            skArc(sketch, "E34.trimOffspring", {"start": v(90.49, 199.32) * mm, "mid": v(89.04, 199.98) * mm, "end": v(87.58, 200.62) * mm});
            skArc(sketch, "E35.trimOffspring", {"start": v(129.95, 176.16) * mm, "mid": v(128.67, 177.1) * mm, "end": v(127.38, 178.03) * mm});
            skArc(sketch, "E36.trimOffspring", {"start": v(163.74, 145.29) * mm, "mid": v(162.68, 146.47) * mm, "end": v(161.6, 147.65) * mm});
            skArc(sketch, "E37.trimOffspring", {"start": v(190.37, 108.07) * mm, "mid": v(189.58, 109.45) * mm, "end": v(188.77, 110.83) * mm});
            skArc(sketch, "E38.trimOffspring", {"start": v(208.68, 66.13) * mm, "mid": v(208.19, 67.64) * mm, "end": v(207.7, 69.16) * mm});
            skArc(sketch, "E39.trimOffspring", {"start": v(217.86, 21.3) * mm, "mid": v(217.7, 22.88) * mm, "end": v(217.53, 24.47) * mm});
            skArc(sketch, "E40.trimOffspring", {"start": v(217.53, -24.47) * mm, "mid": v(217.7, -22.88) * mm, "end": v(217.86, -21.3) * mm});
            skArc(sketch, "E41.trimOffspring", {"start": v(207.7, -69.16) * mm, "mid": v(208.19, -67.64) * mm, "end": v(208.68, -66.13) * mm});
            skArc(sketch, "E42.trimOffspring", {"start": v(188.77, -110.83) * mm, "mid": v(189.58, -109.45) * mm, "end": v(190.37, -108.07) * mm});
            skArc(sketch, "E43.trimOffspring", {"start": v(-190.37, -108.07) * mm, "mid": v(-189.58, -109.45) * mm, "end": v(-188.77, -110.83) * mm});
            skArc(sketch, "E44.trimOffspring", {"start": v(-163.74, -145.29) * mm, "mid": v(-162.68, -146.47) * mm, "end": v(-161.6, -147.65) * mm});
            skArc(sketch, "E45.trimOffspring", {"start": v(-129.95, -176.16) * mm, "mid": v(-128.67, -177.1) * mm, "end": v(-127.38, -178.03) * mm});
            skArc(sketch, "E46.trimOffspring", {"start": v(-90.49, -199.32) * mm, "mid": v(-89.04, -199.98) * mm, "end": v(-87.58, -200.62) * mm});
            skArc(sketch, "E47.trimOffspring", {"start": v(-47.07, -213.78) * mm, "mid": v(-45.51, -214.12) * mm, "end": v(-43.95, -214.45) * mm});
            skArc(sketch, "E48.trimOffspring", {"start": v(-1.6, -218.9) * mm, "mid": v(0, -218.9) * mm, "end": v(1.6, -218.9) * mm});
            skArc(sketch, "E49.trimOffspring", {"start": v(43.95, -214.45) * mm, "mid": v(45.51, -214.12) * mm, "end": v(47.07, -213.78) * mm});
            skArc(sketch, "E50.trimOffspring", {"start": v(87.58, -200.62) * mm, "mid": v(89.04, -199.98) * mm, "end": v(90.49, -199.32) * mm});
            skArc(sketch, "E51.trimOffspring", {"start": v(127.38, -178.03) * mm, "mid": v(128.67, -177.1) * mm, "end": v(129.95, -176.16) * mm});
            skArc(sketch, "E52.trimOffspring", {"start": v(161.6, -147.65) * mm, "mid": v(162.68, -146.47) * mm, "end": v(163.74, -145.29) * mm});
            skSolve(sketch);
        }
        {
            var Q0;
            Q0=qSketchRegion(id+"F1",true);
            extrude(context, id + "F2", {"entities" : qUnion([Q0]), "depth" : 32 * mm});
        }
        {
            var Q0;
            Q0=qCreatedBy(makeId("Right.planeOp"),FACE);
            var sketch = newSketch(context, id + "F3", { "sketchPlane" : qUnion([Q0])});
            skLineSegment(sketch, "E53.bottom", {"start": v(232.58, 21) * mm, "end": v(253.36, 21) * mm});
            skLineSegment(sketch, "E53.top", {"start": v(232.58, 11) * mm, "end": v(253.36, 11) * mm});
            skLineSegment(sketch, "E53.left", {"start": v(228.08, 16.5) * mm, "end": v(228.08, 15.5) * mm});
            skPoint(sketch, "E54.visualSharp", {"position": v(228.08, 21) * mm});
            skArc(sketch, "E54.filletArc", {"start": v(232.58, 21) * mm, "mid": v(229.4, 19.68) * mm, "end": v(228.08, 16.5) * mm});
            skPoint(sketch, "E55.visualSharp", {"position": v(228.08, 11) * mm});
            skArc(sketch, "E55.filletArc", {"start": v(228.08, 15.5) * mm, "mid": v(229.4, 12.32) * mm, "end": v(232.58, 11) * mm});
            skLineSegment(sketch, "E56", {"start": v(0, 0) * mm, "end": v(0, 49.23) * mm});
            skLineSegment(sketch, "E57", {"start": v(253.36, 21) * mm, "end": v(253.36, 11) * mm});
            skSolve(sketch);
        }
        {
            var Q0;
            Q0=qSketchRegion(id+"F3",true);
            var Q1;
            Q1=qConstructionFilter(qBodyType(qCreatedBy(id+"F3",EDGE),BodyType.WIRE),ConstructionObject.NO);
            var Q2;
            Q2=sQuery(id+"F3.wireOp",EDGE,"E56");
            revolve(context, id + "F4", {"operationType" : NewBodyOperationType.REMOVE, "entities" : qUnion([Q0]), "surfaceEntities" : qUnion([Q1]), "axis" : qUnion([Q2]), "revolveType" : RevolveType.FULL});
        }
        {
            var Q0;
            Q0=makeQuery(id+"F2.opExtrude","CAP_EDGE",EDGE,{"disambiguationData":[OSD([sQuery(id+"F1.wireOp",EDGE,"E22.3.22.0")])],"isStart":false});
            var Q1;
            Q1=makeQuery(id+"F2.opExtrude","CAP_EDGE",EDGE,{"disambiguationData":[OSD([sQuery(id+"F1.wireOp",EDGE,"E22.3.23.0")])],"isStart":false});
            var Q2;
            Q2=makeQuery(id+"F2.opExtrude","CAP_EDGE",EDGE,{"disambiguationData":[OSD([sQuery(id+"F1.wireOp",EDGE,"E22.3.24.0")])],"isStart":false});
            var Q3;
            Q3=makeQuery(id+"F2.opExtrude","CAP_EDGE",EDGE,{"disambiguationData":[OSD([sQuery(id+"F1.wireOp",EDGE,"E22.3.25.0")])],"isStart":false});
            var Q4;
            Q4=makeQuery(id+"F2.opExtrude","CAP_EDGE",EDGE,{"disambiguationData":[OSD([sQuery(id+"F1.wireOp",EDGE,"E22.3.26.0")])],"isStart":false});
            var Q5;
            Q5=makeQuery(id+"F2.opExtrude","CAP_EDGE",EDGE,{"disambiguationData":[OSD([sQuery(id+"F1.wireOp",EDGE,"E22.14.23.0"),sQuery(id+"F1.wireOp",EDGE,"E22.18.23.0")])],"isStart":false});
            var Q6;
            Q6=makeQuery(id+"F2.opExtrude","CAP_EDGE",EDGE,{"disambiguationData":[OSD([sQuery(id+"F1.wireOp",EDGE,"E22.14.24.0"),sQuery(id+"F1.wireOp",EDGE,"E22.18.24.0")])],"isStart":false});
            var Q7;
            Q7=makeQuery(id+"F2.opExtrude","CAP_EDGE",EDGE,{"disambiguationData":[OSD([sQuery(id+"F1.wireOp",EDGE,"E22.14.25.0"),sQuery(id+"F1.wireOp",EDGE,"E22.18.25.0")])],"isStart":false});
            var Q8;
            Q8=makeQuery(id+"F2.opExtrude","CAP_EDGE",EDGE,{"disambiguationData":[OSD([sQuery(id+"F1.wireOp",EDGE,"E22.14.26.0"),sQuery(id+"F1.wireOp",EDGE,"E22.18.26.0")])],"isStart":false});
            var Q9;
            Q9=makeQuery(id+"F2.opExtrude","CAP_EDGE",EDGE,{"disambiguationData":[OSD([sQuery(id+"F1.wireOp",EDGE,"E22.3.27.0")])],"isStart":false});
            var Q10;
            Q10=makeQuery(id+"F2.opExtrude","CAP_EDGE",EDGE,{"disambiguationData":[OSD([sQuery(id+"F1.wireOp",EDGE,"E22.14.27.0"),sQuery(id+"F1.wireOp",EDGE,"E22.18.27.0")])],"isStart":false});
            var Q11;
            Q11=makeQuery(id+"F2.opExtrude","CAP_EDGE",EDGE,{"disambiguationData":[OSD([sQuery(id+"F1.wireOp",EDGE,"E22.14.28.0"),sQuery(id+"F1.wireOp",EDGE,"E22.18.28.0")])],"isStart":false});
            var Q12;
            Q12=makeQuery(id+"F2.opExtrude","CAP_EDGE",EDGE,{"disambiguationData":[OSD([sQuery(id+"F1.wireOp",EDGE,"E22.10.28.0")])],"isStart":false});
            var Q13;
            Q13=makeQuery(id+"F2.opExtrude","CAP_EDGE",EDGE,{"disambiguationData":[OSD([sQuery(id+"F1.wireOp",EDGE,"E22.14.29.0"),sQuery(id+"F1.wireOp",EDGE,"E22.18.29.0")])],"isStart":false});
            var Q14;
            Q14=makeQuery(id+"F2.opExtrude","CAP_EDGE",EDGE,{"disambiguationData":[OSD([sQuery(id+"F1.wireOp",EDGE,"E22.10.29.0")])],"isStart":false});
            var Q15;
            Q15=makeQuery(id+"F2.opExtrude","CAP_EDGE",EDGE,{"disambiguationData":[OSD([sQuery(id+"F1.wireOp",EDGE,"E22.3.29.0")])],"isStart":false});
            var Q16;
            Q16=makeQuery(id+"F2.opExtrude","CAP_EDGE",EDGE,{"disambiguationData":[OSD([sQuery(id+"F1.wireOp",EDGE,"E11.0")])],"isStart":false});
            var Q17;
            Q17=makeQuery(id+"F2.opExtrude","CAP_EDGE",EDGE,{"disambiguationData":[OSD([sQuery(id+"F1.wireOp",EDGE,"E20.1.1")])],"isStart":false});
            var Q18;
            Q18=makeQuery(id+"F2.opExtrude","CAP_EDGE",EDGE,{"disambiguationData":[OSD([sQuery(id+"F1.wireOp",EDGE,"E13.0"),sQuery(id+"F1.wireOp",EDGE,"E16.MirrorCS")])],"isStart":false});
            var Q19;
            Q19=makeQuery(id+"F2.opExtrude","CAP_EDGE",EDGE,{"disambiguationData":[OSD([sQuery(id+"F1.wireOp",EDGE,"E20.1.4"),sQuery(id+"F1.wireOp",EDGE,"E20.1.5")])],"isStart":false});
            var Q20;
            Q20=makeQuery(id+"F2.opExtrude","CAP_EDGE",EDGE,{"disambiguationData":[OSD([sQuery(id+"F1.wireOp",EDGE,"E20.2.4"),sQuery(id+"F1.wireOp",EDGE,"E20.2.5")])],"isStart":false});
            var Q21;
            Q21=makeQuery(id+"F2.opExtrude","CAP_EDGE",EDGE,{"disambiguationData":[OSD([sQuery(id+"F1.wireOp",EDGE,"E20.2.1")])],"isStart":false});
            var Q22;
            Q22=makeQuery(id+"F2.opExtrude","CAP_EDGE",EDGE,{"disambiguationData":[OSD([sQuery(id+"F1.wireOp",EDGE,"E21.14.3.0"),sQuery(id+"F1.wireOp",EDGE,"E21.18.3.0")])],"isStart":false});
            var Q23;
            Q23=makeQuery(id+"F2.opExtrude","CAP_EDGE",EDGE,{"disambiguationData":[OSD([sQuery(id+"F1.wireOp",EDGE,"E21.3.3.0")])],"isStart":false});
            var Q24;
            Q24=makeQuery(id+"F2.opExtrude","CAP_EDGE",EDGE,{"disambiguationData":[OSD([sQuery(id+"F1.wireOp",EDGE,"E21.14.4.0"),sQuery(id+"F1.wireOp",EDGE,"E21.18.4.0")])],"isStart":false});
            var Q25;
            Q25=makeQuery(id+"F2.opExtrude","CAP_EDGE",EDGE,{"disambiguationData":[OSD([sQuery(id+"F1.wireOp",EDGE,"E21.3.4.0")])],"isStart":false});
            var Q26;
            Q26=makeQuery(id+"F2.opExtrude","CAP_EDGE",EDGE,{"disambiguationData":[OSD([sQuery(id+"F1.wireOp",EDGE,"E21.14.5.0"),sQuery(id+"F1.wireOp",EDGE,"E21.18.5.0")])],"isStart":false});
            var Q27;
            Q27=makeQuery(id+"F2.opExtrude","CAP_EDGE",EDGE,{"disambiguationData":[OSD([sQuery(id+"F1.wireOp",EDGE,"E21.3.5.0")])],"isStart":false});
            var Q28;
            Q28=makeQuery(id+"F2.opExtrude","CAP_EDGE",EDGE,{"disambiguationData":[OSD([sQuery(id+"F1.wireOp",EDGE,"E22.14.6.0"),sQuery(id+"F1.wireOp",EDGE,"E22.18.6.0")])],"isStart":false});
            var Q29;
            Q29=makeQuery(id+"F2.opExtrude","CAP_EDGE",EDGE,{"disambiguationData":[OSD([sQuery(id+"F1.wireOp",EDGE,"E22.3.6.0")])],"isStart":false});
            var Q30;
            Q30=makeQuery(id+"F2.opExtrude","CAP_EDGE",EDGE,{"disambiguationData":[OSD([sQuery(id+"F1.wireOp",EDGE,"E22.14.7.0"),sQuery(id+"F1.wireOp",EDGE,"E22.18.7.0")])],"isStart":false});
            var Q31;
            Q31=makeQuery(id+"F2.opExtrude","CAP_EDGE",EDGE,{"disambiguationData":[OSD([sQuery(id+"F1.wireOp",EDGE,"E22.3.7.0")])],"isStart":false});
            var Q32;
            Q32=makeQuery(id+"F2.opExtrude","CAP_EDGE",EDGE,{"disambiguationData":[OSD([sQuery(id+"F1.wireOp",EDGE,"E22.14.8.0"),sQuery(id+"F1.wireOp",EDGE,"E22.18.8.0")])],"isStart":false});
            var Q33;
            Q33=makeQuery(id+"F2.opExtrude","CAP_EDGE",EDGE,{"disambiguationData":[OSD([sQuery(id+"F1.wireOp",EDGE,"E22.3.8.0")])],"isStart":false});
            var Q34;
            Q34=makeQuery(id+"F2.opExtrude","CAP_EDGE",EDGE,{"disambiguationData":[OSD([sQuery(id+"F1.wireOp",EDGE,"E22.14.9.0"),sQuery(id+"F1.wireOp",EDGE,"E22.18.9.0")])],"isStart":false});
            var Q35;
            Q35=makeQuery(id+"F2.opExtrude","CAP_EDGE",EDGE,{"disambiguationData":[OSD([sQuery(id+"F1.wireOp",EDGE,"E22.3.9.0")])],"isStart":false});
            var Q36;
            Q36=makeQuery(id+"F2.opExtrude","CAP_EDGE",EDGE,{"disambiguationData":[OSD([sQuery(id+"F1.wireOp",EDGE,"E22.14.10.0"),sQuery(id+"F1.wireOp",EDGE,"E22.18.10.0")])],"isStart":false});
            var Q37;
            Q37=makeQuery(id+"F2.opExtrude","CAP_EDGE",EDGE,{"disambiguationData":[OSD([sQuery(id+"F1.wireOp",EDGE,"E22.3.10.0")])],"isStart":false});
            var Q38;
            Q38=makeQuery(id+"F2.opExtrude","CAP_EDGE",EDGE,{"disambiguationData":[OSD([sQuery(id+"F1.wireOp",EDGE,"E22.3.11.0")])],"isStart":false});
            var Q39;
            Q39=makeQuery(id+"F2.opExtrude","CAP_EDGE",EDGE,{"disambiguationData":[OSD([sQuery(id+"F1.wireOp",EDGE,"E22.14.12.0"),sQuery(id+"F1.wireOp",EDGE,"E22.18.12.0")])],"isStart":false});
            var Q40;
            Q40=makeQuery(id+"F2.opExtrude","CAP_EDGE",EDGE,{"disambiguationData":[OSD([sQuery(id+"F1.wireOp",EDGE,"E22.3.12.0")])],"isStart":false});
            var Q41;
            Q41=makeQuery(id+"F2.opExtrude","CAP_EDGE",EDGE,{"disambiguationData":[OSD([sQuery(id+"F1.wireOp",EDGE,"E22.14.13.0"),sQuery(id+"F1.wireOp",EDGE,"E22.18.13.0")])],"isStart":false});
            var Q42;
            Q42=makeQuery(id+"F2.opExtrude","CAP_EDGE",EDGE,{"disambiguationData":[OSD([sQuery(id+"F1.wireOp",EDGE,"E22.3.13.0")])],"isStart":false});
            var Q43;
            Q43=makeQuery(id+"F2.opExtrude","CAP_EDGE",EDGE,{"disambiguationData":[OSD([sQuery(id+"F1.wireOp",EDGE,"E22.14.14.0"),sQuery(id+"F1.wireOp",EDGE,"E22.18.14.0")])],"isStart":false});
            var Q44;
            Q44=makeQuery(id+"F2.opExtrude","CAP_EDGE",EDGE,{"disambiguationData":[OSD([sQuery(id+"F1.wireOp",EDGE,"E22.3.14.0")])],"isStart":false});
            var Q45;
            Q45=makeQuery(id+"F2.opExtrude","CAP_EDGE",EDGE,{"disambiguationData":[OSD([sQuery(id+"F1.wireOp",EDGE,"E22.14.15.0"),sQuery(id+"F1.wireOp",EDGE,"E22.18.15.0")])],"isStart":false});
            var Q46;
            Q46=makeQuery(id+"F2.opExtrude","CAP_EDGE",EDGE,{"disambiguationData":[OSD([sQuery(id+"F1.wireOp",EDGE,"E22.3.15.0")])],"isStart":false});
            var Q47;
            Q47=makeQuery(id+"F2.opExtrude","CAP_EDGE",EDGE,{"disambiguationData":[OSD([sQuery(id+"F1.wireOp",EDGE,"E22.14.16.0"),sQuery(id+"F1.wireOp",EDGE,"E22.18.16.0")])],"isStart":false});
            var Q48;
            Q48=makeQuery(id+"F2.opExtrude","CAP_EDGE",EDGE,{"disambiguationData":[OSD([sQuery(id+"F1.wireOp",EDGE,"E22.3.16.0")])],"isStart":false});
            var Q49;
            Q49=makeQuery(id+"F2.opExtrude","CAP_EDGE",EDGE,{"disambiguationData":[OSD([sQuery(id+"F1.wireOp",EDGE,"E22.14.17.0"),sQuery(id+"F1.wireOp",EDGE,"E22.18.17.0")])],"isStart":false});
            var Q50;
            Q50=makeQuery(id+"F2.opExtrude","CAP_EDGE",EDGE,{"disambiguationData":[OSD([sQuery(id+"F1.wireOp",EDGE,"E22.3.17.0")])],"isStart":false});
            var Q51;
            Q51=makeQuery(id+"F2.opExtrude","CAP_EDGE",EDGE,{"disambiguationData":[OSD([sQuery(id+"F1.wireOp",EDGE,"E22.14.18.0"),sQuery(id+"F1.wireOp",EDGE,"E22.18.18.0")])],"isStart":false});
            var Q52;
            Q52=makeQuery(id+"F2.opExtrude","CAP_EDGE",EDGE,{"disambiguationData":[OSD([sQuery(id+"F1.wireOp",EDGE,"E22.3.18.0")])],"isStart":false});
            var Q53;
            Q53=makeQuery(id+"F2.opExtrude","CAP_EDGE",EDGE,{"disambiguationData":[OSD([sQuery(id+"F1.wireOp",EDGE,"E22.14.19.0"),sQuery(id+"F1.wireOp",EDGE,"E22.18.19.0")])],"isStart":false});
            var Q54;
            Q54=makeQuery(id+"F2.opExtrude","CAP_EDGE",EDGE,{"disambiguationData":[OSD([sQuery(id+"F1.wireOp",EDGE,"E22.3.19.0")])],"isStart":false});
            var Q55;
            Q55=makeQuery(id+"F2.opExtrude","CAP_EDGE",EDGE,{"disambiguationData":[OSD([sQuery(id+"F1.wireOp",EDGE,"E22.14.20.0"),sQuery(id+"F1.wireOp",EDGE,"E22.18.20.0")])],"isStart":false});
            var Q56;
            Q56=makeQuery(id+"F2.opExtrude","CAP_EDGE",EDGE,{"disambiguationData":[OSD([sQuery(id+"F1.wireOp",EDGE,"E22.3.20.0")])],"isStart":false});
            var Q57;
            Q57=makeQuery(id+"F2.opExtrude","CAP_EDGE",EDGE,{"disambiguationData":[OSD([sQuery(id+"F1.wireOp",EDGE,"E22.14.21.0"),sQuery(id+"F1.wireOp",EDGE,"E22.18.21.0")])],"isStart":false});
            var Q58;
            Q58=makeQuery(id+"F2.opExtrude","CAP_EDGE",EDGE,{"disambiguationData":[OSD([sQuery(id+"F1.wireOp",EDGE,"E22.3.21.0")])],"isStart":false});
            var Q59;
            Q59=makeQuery(id+"F2.opExtrude","CAP_EDGE",EDGE,{"disambiguationData":[OSD([sQuery(id+"F1.wireOp",EDGE,"E22.14.22.0"),sQuery(id+"F1.wireOp",EDGE,"E22.18.22.0")])],"isStart":false});
            var Q60;
            Q60=makeQuery(id+"F2.opExtrude","CAP_EDGE",EDGE,{"disambiguationData":[OSD([sQuery(id+"F1.wireOp",EDGE,"E22.14.10.0"),sQuery(id+"F1.wireOp",EDGE,"E22.18.10.0")])],"isStart":true});
            var Q61;
            Q61=makeQuery(id+"F2.opExtrude","CAP_EDGE",EDGE,{"disambiguationData":[OSD([sQuery(id+"F1.wireOp",EDGE,"E22.29.10.0")])],"isStart":true});
            var Q62;
            Q62=makeQuery(id+"F2.opExtrude","CAP_EDGE",EDGE,{"disambiguationData":[OSD([sQuery(id+"F1.wireOp",EDGE,"E22.14.9.0"),sQuery(id+"F1.wireOp",EDGE,"E22.18.9.0")])],"isStart":true});
            var Q63;
            Q63=makeQuery(id+"F2.opExtrude","CAP_EDGE",EDGE,{"disambiguationData":[OSD([sQuery(id+"F1.wireOp",EDGE,"E22.29.9.0")])],"isStart":true});
            var Q64;
            Q64=makeQuery(id+"F2.opExtrude","CAP_EDGE",EDGE,{"disambiguationData":[OSD([sQuery(id+"F1.wireOp",EDGE,"E22.14.8.0"),sQuery(id+"F1.wireOp",EDGE,"E22.18.8.0")])],"isStart":true});
            var Q65;
            Q65=makeQuery(id+"F2.opExtrude","CAP_EDGE",EDGE,{"disambiguationData":[OSD([sQuery(id+"F1.wireOp",EDGE,"E22.29.8.0")])],"isStart":true});
            var Q66;
            Q66=makeQuery(id+"F2.opExtrude","CAP_EDGE",EDGE,{"disambiguationData":[OSD([sQuery(id+"F1.wireOp",EDGE,"E22.14.7.0"),sQuery(id+"F1.wireOp",EDGE,"E22.18.7.0")])],"isStart":true});
            var Q67;
            Q67=makeQuery(id+"F2.opExtrude","CAP_EDGE",EDGE,{"disambiguationData":[OSD([sQuery(id+"F1.wireOp",EDGE,"E22.29.7.0")])],"isStart":true});
            var Q68;
            Q68=makeQuery(id+"F2.opExtrude","CAP_EDGE",EDGE,{"disambiguationData":[OSD([sQuery(id+"F1.wireOp",EDGE,"E22.14.6.0"),sQuery(id+"F1.wireOp",EDGE,"E22.18.6.0")])],"isStart":true});
            var Q69;
            Q69=makeQuery(id+"F2.opExtrude","CAP_EDGE",EDGE,{"disambiguationData":[OSD([sQuery(id+"F1.wireOp",EDGE,"E22.29.6.0")])],"isStart":true});
            var Q70;
            Q70=makeQuery(id+"F2.opExtrude","CAP_EDGE",EDGE,{"disambiguationData":[OSD([sQuery(id+"F1.wireOp",EDGE,"E21.14.5.0"),sQuery(id+"F1.wireOp",EDGE,"E21.18.5.0")])],"isStart":true});
            var Q71;
            Q71=makeQuery(id+"F2.opExtrude","CAP_EDGE",EDGE,{"disambiguationData":[OSD([sQuery(id+"F1.wireOp",EDGE,"E21.29.5.0")])],"isStart":true});
            var Q72;
            Q72=makeQuery(id+"F2.opExtrude","CAP_EDGE",EDGE,{"disambiguationData":[OSD([sQuery(id+"F1.wireOp",EDGE,"E21.14.4.0"),sQuery(id+"F1.wireOp",EDGE,"E21.18.4.0")])],"isStart":true});
            var Q73;
            Q73=makeQuery(id+"F2.opExtrude","CAP_EDGE",EDGE,{"disambiguationData":[OSD([sQuery(id+"F1.wireOp",EDGE,"E21.29.4.0")])],"isStart":true});
            var Q74;
            Q74=makeQuery(id+"F2.opExtrude","CAP_EDGE",EDGE,{"disambiguationData":[OSD([sQuery(id+"F1.wireOp",EDGE,"E21.14.3.0"),sQuery(id+"F1.wireOp",EDGE,"E21.18.3.0")])],"isStart":true});
            var Q75;
            Q75=makeQuery(id+"F2.opExtrude","CAP_EDGE",EDGE,{"disambiguationData":[OSD([sQuery(id+"F1.wireOp",EDGE,"E21.29.3.0")])],"isStart":true});
            var Q76;
            Q76=makeQuery(id+"F2.opExtrude","CAP_EDGE",EDGE,{"disambiguationData":[OSD([sQuery(id+"F1.wireOp",EDGE,"E20.2.4"),sQuery(id+"F1.wireOp",EDGE,"E20.2.5")])],"isStart":true});
            var Q77;
            Q77=makeQuery(id+"F2.opExtrude","CAP_EDGE",EDGE,{"disambiguationData":[OSD([sQuery(id+"F1.wireOp",EDGE,"E20.2.8")])],"isStart":true});
            var Q78;
            Q78=makeQuery(id+"F2.opExtrude","CAP_EDGE",EDGE,{"disambiguationData":[OSD([sQuery(id+"F1.wireOp",EDGE,"E20.1.4"),sQuery(id+"F1.wireOp",EDGE,"E20.1.5")])],"isStart":true});
            var Q79;
            Q79=makeQuery(id+"F2.opExtrude","CAP_EDGE",EDGE,{"disambiguationData":[OSD([sQuery(id+"F1.wireOp",EDGE,"E20.1.8")])],"isStart":true});
            var Q80;
            Q80=makeQuery(id+"F2.opExtrude","CAP_EDGE",EDGE,{"disambiguationData":[OSD([sQuery(id+"F1.wireOp",EDGE,"E13.0"),sQuery(id+"F1.wireOp",EDGE,"E16.MirrorCS")])],"isStart":true});
            var Q81;
            Q81=makeQuery(id+"F2.opExtrude","CAP_EDGE",EDGE,{"disambiguationData":[OSD([sQuery(id+"F1.wireOp",EDGE,"E19.MirrorCS")])],"isStart":true});
            var Q82;
            Q82=makeQuery(id+"F2.opExtrude","CAP_EDGE",EDGE,{"disambiguationData":[OSD([sQuery(id+"F1.wireOp",EDGE,"E22.14.29.0"),sQuery(id+"F1.wireOp",EDGE,"E22.18.29.0")])],"isStart":true});
            var Q83;
            Q83=makeQuery(id+"F2.opExtrude","CAP_EDGE",EDGE,{"disambiguationData":[OSD([sQuery(id+"F1.wireOp",EDGE,"E22.29.29.0")])],"isStart":true});
            var Q84;
            Q84=makeQuery(id+"F2.opExtrude","CAP_EDGE",EDGE,{"disambiguationData":[OSD([sQuery(id+"F1.wireOp",EDGE,"E22.14.28.0"),sQuery(id+"F1.wireOp",EDGE,"E22.18.28.0")])],"isStart":true});
            var Q85;
            Q85=makeQuery(id+"F2.opExtrude","CAP_EDGE",EDGE,{"disambiguationData":[OSD([sQuery(id+"F1.wireOp",EDGE,"E22.29.28.0")])],"isStart":true});
            var Q86;
            Q86=makeQuery(id+"F2.opExtrude","CAP_EDGE",EDGE,{"disambiguationData":[OSD([sQuery(id+"F1.wireOp",EDGE,"E22.14.27.0"),sQuery(id+"F1.wireOp",EDGE,"E22.18.27.0")])],"isStart":true});
            var Q87;
            Q87=makeQuery(id+"F2.opExtrude","CAP_EDGE",EDGE,{"disambiguationData":[OSD([sQuery(id+"F1.wireOp",EDGE,"E22.29.27.0")])],"isStart":true});
            var Q88;
            Q88=makeQuery(id+"F2.opExtrude","CAP_EDGE",EDGE,{"disambiguationData":[OSD([sQuery(id+"F1.wireOp",EDGE,"E22.29.26.0")])],"isStart":true});
            var Q89;
            Q89=makeQuery(id+"F2.opExtrude","CAP_EDGE",EDGE,{"disambiguationData":[OSD([sQuery(id+"F1.wireOp",EDGE,"E22.14.26.0"),sQuery(id+"F1.wireOp",EDGE,"E22.18.26.0")])],"isStart":true});
            var Q90;
            Q90=makeQuery(id+"F2.opExtrude","CAP_EDGE",EDGE,{"disambiguationData":[OSD([sQuery(id+"F1.wireOp",EDGE,"E22.14.25.0"),sQuery(id+"F1.wireOp",EDGE,"E22.18.25.0")])],"isStart":true});
            var Q91;
            Q91=makeQuery(id+"F2.opExtrude","CAP_EDGE",EDGE,{"disambiguationData":[OSD([sQuery(id+"F1.wireOp",EDGE,"E22.29.25.0")])],"isStart":true});
            var Q92;
            Q92=makeQuery(id+"F2.opExtrude","CAP_EDGE",EDGE,{"disambiguationData":[OSD([sQuery(id+"F1.wireOp",EDGE,"E22.14.24.0"),sQuery(id+"F1.wireOp",EDGE,"E22.18.24.0")])],"isStart":true});
            var Q93;
            Q93=makeQuery(id+"F2.opExtrude","CAP_EDGE",EDGE,{"disambiguationData":[OSD([sQuery(id+"F1.wireOp",EDGE,"E22.29.24.0")])],"isStart":true});
            var Q94;
            Q94=makeQuery(id+"F2.opExtrude","CAP_EDGE",EDGE,{"disambiguationData":[OSD([sQuery(id+"F1.wireOp",EDGE,"E22.14.23.0"),sQuery(id+"F1.wireOp",EDGE,"E22.18.23.0")])],"isStart":true});
            var Q95;
            Q95=makeQuery(id+"F2.opExtrude","CAP_EDGE",EDGE,{"disambiguationData":[OSD([sQuery(id+"F1.wireOp",EDGE,"E22.29.23.0")])],"isStart":true});
            var Q96;
            Q96=makeQuery(id+"F2.opExtrude","CAP_EDGE",EDGE,{"disambiguationData":[OSD([sQuery(id+"F1.wireOp",EDGE,"E22.14.22.0"),sQuery(id+"F1.wireOp",EDGE,"E22.18.22.0")])],"isStart":true});
            var Q97;
            Q97=makeQuery(id+"F2.opExtrude","CAP_EDGE",EDGE,{"disambiguationData":[OSD([sQuery(id+"F1.wireOp",EDGE,"E22.14.21.0"),sQuery(id+"F1.wireOp",EDGE,"E22.18.21.0")])],"isStart":true});
            var Q98;
            Q98=makeQuery(id+"F2.opExtrude","CAP_EDGE",EDGE,{"disambiguationData":[OSD([sQuery(id+"F1.wireOp",EDGE,"E22.29.21.0")])],"isStart":true});
            var Q99;
            Q99=makeQuery(id+"F2.opExtrude","CAP_EDGE",EDGE,{"disambiguationData":[OSD([sQuery(id+"F1.wireOp",EDGE,"E22.14.20.0"),sQuery(id+"F1.wireOp",EDGE,"E22.18.20.0")])],"isStart":true});
            var Q100;
            Q100=makeQuery(id+"F2.opExtrude","CAP_EDGE",EDGE,{"disambiguationData":[OSD([sQuery(id+"F1.wireOp",EDGE,"E22.29.20.0")])],"isStart":true});
            var Q101;
            Q101=makeQuery(id+"F2.opExtrude","CAP_EDGE",EDGE,{"disambiguationData":[OSD([sQuery(id+"F1.wireOp",EDGE,"E22.14.19.0"),sQuery(id+"F1.wireOp",EDGE,"E22.18.19.0")])],"isStart":true});
            var Q102;
            Q102=makeQuery(id+"F2.opExtrude","CAP_EDGE",EDGE,{"disambiguationData":[OSD([sQuery(id+"F1.wireOp",EDGE,"E22.29.19.0")])],"isStart":true});
            var Q103;
            Q103=makeQuery(id+"F2.opExtrude","CAP_EDGE",EDGE,{"disambiguationData":[OSD([sQuery(id+"F1.wireOp",EDGE,"E22.14.18.0"),sQuery(id+"F1.wireOp",EDGE,"E22.18.18.0")])],"isStart":true});
            var Q104;
            Q104=makeQuery(id+"F2.opExtrude","CAP_EDGE",EDGE,{"disambiguationData":[OSD([sQuery(id+"F1.wireOp",EDGE,"E22.29.18.0")])],"isStart":true});
            var Q105;
            Q105=makeQuery(id+"F2.opExtrude","CAP_EDGE",EDGE,{"disambiguationData":[OSD([sQuery(id+"F1.wireOp",EDGE,"E22.14.17.0"),sQuery(id+"F1.wireOp",EDGE,"E22.18.17.0")])],"isStart":true});
            var Q106;
            Q106=makeQuery(id+"F2.opExtrude","CAP_EDGE",EDGE,{"disambiguationData":[OSD([sQuery(id+"F1.wireOp",EDGE,"E22.29.17.0")])],"isStart":true});
            var Q107;
            Q107=makeQuery(id+"F2.opExtrude","CAP_EDGE",EDGE,{"disambiguationData":[OSD([sQuery(id+"F1.wireOp",EDGE,"E22.14.16.0"),sQuery(id+"F1.wireOp",EDGE,"E22.18.16.0")])],"isStart":true});
            var Q108;
            Q108=makeQuery(id+"F2.opExtrude","CAP_EDGE",EDGE,{"disambiguationData":[OSD([sQuery(id+"F1.wireOp",EDGE,"E22.29.16.0")])],"isStart":true});
            var Q109;
            Q109=makeQuery(id+"F2.opExtrude","CAP_EDGE",EDGE,{"disambiguationData":[OSD([sQuery(id+"F1.wireOp",EDGE,"E22.14.15.0"),sQuery(id+"F1.wireOp",EDGE,"E22.18.15.0")])],"isStart":true});
            var Q110;
            Q110=makeQuery(id+"F2.opExtrude","CAP_EDGE",EDGE,{"disambiguationData":[OSD([sQuery(id+"F1.wireOp",EDGE,"E22.29.15.0")])],"isStart":true});
            var Q111;
            Q111=makeQuery(id+"F2.opExtrude","CAP_EDGE",EDGE,{"disambiguationData":[OSD([sQuery(id+"F1.wireOp",EDGE,"E22.14.14.0"),sQuery(id+"F1.wireOp",EDGE,"E22.18.14.0")])],"isStart":true});
            var Q112;
            Q112=makeQuery(id+"F2.opExtrude","CAP_EDGE",EDGE,{"disambiguationData":[OSD([sQuery(id+"F1.wireOp",EDGE,"E22.29.14.0")])],"isStart":true});
            var Q113;
            Q113=makeQuery(id+"F2.opExtrude","CAP_EDGE",EDGE,{"disambiguationData":[OSD([sQuery(id+"F1.wireOp",EDGE,"E22.14.13.0"),sQuery(id+"F1.wireOp",EDGE,"E22.18.13.0")])],"isStart":true});
            var Q114;
            Q114=makeQuery(id+"F2.opExtrude","CAP_EDGE",EDGE,{"disambiguationData":[OSD([sQuery(id+"F1.wireOp",EDGE,"E22.29.13.0")])],"isStart":true});
            var Q115;
            Q115=makeQuery(id+"F2.opExtrude","CAP_EDGE",EDGE,{"disambiguationData":[OSD([sQuery(id+"F1.wireOp",EDGE,"E22.14.12.0"),sQuery(id+"F1.wireOp",EDGE,"E22.18.12.0")])],"isStart":true});
            var Q116;
            Q116=makeQuery(id+"F2.opExtrude","CAP_EDGE",EDGE,{"disambiguationData":[OSD([sQuery(id+"F1.wireOp",EDGE,"E22.29.12.0")])],"isStart":true});
            var Q117;
            Q117=makeQuery(id+"F2.opExtrude","CAP_EDGE",EDGE,{"disambiguationData":[OSD([sQuery(id+"F1.wireOp",EDGE,"E22.14.11.0"),sQuery(id+"F1.wireOp",EDGE,"E22.18.11.0")])],"isStart":true});
            var Q118;
            Q118=makeQuery(id+"F2.opExtrude","CAP_EDGE",EDGE,{"disambiguationData":[OSD([sQuery(id+"F1.wireOp",EDGE,"E22.29.11.0")])],"isStart":true});
            var Q119;
            Q119=makeQuery(id+"F2.opExtrude","CAP_EDGE",EDGE,{"disambiguationData":[OSD([sQuery(id+"F1.wireOp",EDGE,"E22.3.10.0")])],"isStart":true});
            chamfer(context, id + "F5", {"entities" : qUnion([Q0, Q1, Q2, Q3, Q4, Q5, Q6, Q7, Q8, Q9, Q10, Q11, Q12, Q13, Q14, Q15, Q16, Q17, Q18, Q19, Q20, Q21, Q22, Q23, Q24, Q25, Q26, Q27, Q28, Q29, Q30, Q31, Q32, Q33, Q34, Q35, Q36, Q37, Q38, Q39, Q40, Q41, Q42, Q43, Q44, Q45, Q46, Q47, Q48, Q49, Q50, Q51, Q52, Q53, Q54, Q55, Q56, Q57, Q58, Q59, Q60, Q61, Q62, Q63, Q64, Q65, Q66, Q67, Q68, Q69, Q70, Q71, Q72, Q73, Q74, Q75, Q76, Q77, Q78, Q79, Q80, Q81, Q82, Q83, Q84, Q85, Q86, Q87, Q88, Q89, Q90, Q91, Q92, Q93, Q94, Q95, Q96, Q97, Q98, Q99, Q100, Q101, Q102, Q103, Q104, Q105, Q106, Q107, Q108, Q109, Q110, Q111, Q112, Q113, Q114, Q115, Q116, Q117, Q118, Q119]), "chamferType" : ChamferType.OFFSET_ANGLE, "width" : 2 * mm, "oppositeDirection" : false, "angle" : 45 * degree, "tangentPropagation" : true});
        }
        {
            var Q0;
            Q0=qCreatedBy(makeId("Top.planeOp"),FACE);
            var sketch = newSketch(context, id + "F6", { "sketchPlane" : qUnion([Q0])});
            skCircle(sketch, "E58", {"center": v(0, 0) * mm, "radius": 45 * mm});
            skSolve(sketch);
        }
        {
            var Q0;
            Q0=qSketchRegion(id+"F6",true);
            extrude(context, id + "F7", {"entities" : qUnion([Q0]), "operationType" : NewBodyOperationType.REMOVE, "oppositeDirection" : true, "depth" : 50 * mm, "hasSecondDirection" : true, "secondDirectionOppositeDirection" : false, "secondDirectionDepth" : 69.89 * mm});
        }
        {
            var Q0;
            Q0=makeQuery(id+"F7.boolean.opBoolean","INTERSECT",EDGE,{"derivedFrom":[makeQuery(id+"F2.opExtrude","CAP_FACE",FACE,{"disambiguationData":[OSD([sQuery(id+"F1.wireOp",EDGE,"E11.0"),sQuery(id+"F1.wireOp",EDGE,"E12.0"),sQuery(id+"F1.wireOp",EDGE,"E13.0"),sQuery(id+"F1.wireOp",EDGE,"E15.0"),sQuery(id+"F1.wireOp",EDGE,"E16.MirrorCS"),sQuery(id+"F1.wireOp",EDGE,"E17.MirrorCS"),sQuery(id+"F1.wireOp",EDGE,"E18.MirrorCS"),sQuery(id+"F1.wireOp",EDGE,"E19.MirrorCS"),sQuery(id+"F1.wireOp",EDGE,"E20.1.1"),sQuery(id+"F1.wireOp",EDGE,"E20.1.2"),sQuery(id+"F1.wireOp",EDGE,"E20.1.3"),sQuery(id+"F1.wireOp",EDGE,"E20.1.4"),sQuery(id+"F1.wireOp",EDGE,"E20.1.5"),sQuery(id+"F1.wireOp",EDGE,"E20.1.6"),sQuery(id+"F1.wireOp",EDGE,"E20.1.7"),sQuery(id+"F1.wireOp",EDGE,"E20.1.8"),sQuery(id+"F1.wireOp",EDGE,"E20.2.1"),sQuery(id+"F1.wireOp",EDGE,"E20.2.2"),sQuery(id+"F1.wireOp",EDGE,"E20.2.3"),sQuery(id+"F1.wireOp",EDGE,"E20.2.4"),sQuery(id+"F1.wireOp",EDGE,"E20.2.5"),sQuery(id+"F1.wireOp",EDGE,"E20.2.6"),sQuery(id+"F1.wireOp",EDGE,"E20.2.7"),sQuery(id+"F1.wireOp",EDGE,"E20.2.8"),sQuery(id+"F1.wireOp",EDGE,"E21.3.3.0"),sQuery(id+"F1.wireOp",EDGE,"E21.7.3.0"),sQuery(id+"F1.wireOp",EDGE,"E21.10.3.0"),sQuery(id+"F1.wireOp",EDGE,"E21.14.3.0"),sQuery(id+"F1.wireOp",EDGE,"E21.18.3.0"),sQuery(id+"F1.wireOp",EDGE,"E21.22.3.0"),sQuery(id+"F1.wireOp",EDGE,"E21.26.3.0"),sQuery(id+"F1.wireOp",EDGE,"E21.29.3.0"),sQuery(id+"F1.wireOp",EDGE,"E21.3.4.0"),sQuery(id+"F1.wireOp",EDGE,"E21.7.4.0"),sQuery(id+"F1.wireOp",EDGE,"E21.10.4.0"),sQuery(id+"F1.wireOp",EDGE,"E21.14.4.0"),sQuery(id+"F1.wireOp",EDGE,"E21.18.4.0"),sQuery(id+"F1.wireOp",EDGE,"E21.22.4.0"),sQuery(id+"F1.wireOp",EDGE,"E21.26.4.0"),sQuery(id+"F1.wireOp",EDGE,"E21.29.4.0"),sQuery(id+"F1.wireOp",EDGE,"E21.3.5.0"),sQuery(id+"F1.wireOp",EDGE,"E21.7.5.0"),sQuery(id+"F1.wireOp",EDGE,"E21.10.5.0"),sQuery(id+"F1.wireOp",EDGE,"E21.14.5.0"),sQuery(id+"F1.wireOp",EDGE,"E21.18.5.0"),sQuery(id+"F1.wireOp",EDGE,"E21.22.5.0"),sQuery(id+"F1.wireOp",EDGE,"E21.26.5.0"),sQuery(id+"F1.wireOp",EDGE,"E21.29.5.0"),sQuery(id+"F1.wireOp",EDGE,"E22.3.6.0"),sQuery(id+"F1.wireOp",EDGE,"E22.7.6.0"),sQuery(id+"F1.wireOp",EDGE,"E22.10.6.0"),sQuery(id+"F1.wireOp",EDGE,"E22.14.6.0"),sQuery(id+"F1.wireOp",EDGE,"E22.18.6.0"),sQuery(id+"F1.wireOp",EDGE,"E22.22.6.0"),sQuery(id+"F1.wireOp",EDGE,"E22.26.6.0"),sQuery(id+"F1.wireOp",EDGE,"E22.29.6.0"),sQuery(id+"F1.wireOp",EDGE,"E22.3.7.0"),sQuery(id+"F1.wireOp",EDGE,"E22.7.7.0"),sQuery(id+"F1.wireOp",EDGE,"E22.10.7.0"),sQuery(id+"F1.wireOp",EDGE,"E22.14.7.0"),sQuery(id+"F1.wireOp",EDGE,"E22.18.7.0"),sQuery(id+"F1.wireOp",EDGE,"E22.22.7.0"),sQuery(id+"F1.wireOp",EDGE,"E22.26.7.0"),sQuery(id+"F1.wireOp",EDGE,"E22.29.7.0"),sQuery(id+"F1.wireOp",EDGE,"E22.3.8.0"),sQuery(id+"F1.wireOp",EDGE,"E22.7.8.0"),sQuery(id+"F1.wireOp",EDGE,"E22.10.8.0"),sQuery(id+"F1.wireOp",EDGE,"E22.14.8.0"),sQuery(id+"F1.wireOp",EDGE,"E22.18.8.0"),sQuery(id+"F1.wireOp",EDGE,"E22.22.8.0"),sQuery(id+"F1.wireOp",EDGE,"E22.26.8.0"),sQuery(id+"F1.wireOp",EDGE,"E22.29.8.0"),sQuery(id+"F1.wireOp",EDGE,"E22.3.9.0"),sQuery(id+"F1.wireOp",EDGE,"E22.7.9.0"),sQuery(id+"F1.wireOp",EDGE,"E22.10.9.0"),sQuery(id+"F1.wireOp",EDGE,"E22.14.9.0"),sQuery(id+"F1.wireOp",EDGE,"E22.18.9.0"),sQuery(id+"F1.wireOp",EDGE,"E22.22.9.0"),sQuery(id+"F1.wireOp",EDGE,"E22.26.9.0"),sQuery(id+"F1.wireOp",EDGE,"E22.29.9.0"),sQuery(id+"F1.wireOp",EDGE,"E22.3.10.0"),sQuery(id+"F1.wireOp",EDGE,"E22.7.10.0"),sQuery(id+"F1.wireOp",EDGE,"E22.10.10.0"),sQuery(id+"F1.wireOp",EDGE,"E22.14.10.0"),sQuery(id+"F1.wireOp",EDGE,"E22.18.10.0"),sQuery(id+"F1.wireOp",EDGE,"E22.22.10.0"),sQuery(id+"F1.wireOp",EDGE,"E22.26.10.0"),sQuery(id+"F1.wireOp",EDGE,"E22.29.10.0"),sQuery(id+"F1.wireOp",EDGE,"E22.3.11.0"),sQuery(id+"F1.wireOp",EDGE,"E22.7.11.0"),sQuery(id+"F1.wireOp",EDGE,"E22.10.11.0"),sQuery(id+"F1.wireOp",EDGE,"E22.14.11.0"),sQuery(id+"F1.wireOp",EDGE,"E22.18.11.0"),sQuery(id+"F1.wireOp",EDGE,"E22.22.11.0"),sQuery(id+"F1.wireOp",EDGE,"E22.26.11.0"),sQuery(id+"F1.wireOp",EDGE,"E22.29.11.0"),sQuery(id+"F1.wireOp",EDGE,"E22.3.12.0"),sQuery(id+"F1.wireOp",EDGE,"E22.7.12.0"),sQuery(id+"F1.wireOp",EDGE,"E22.10.12.0"),sQuery(id+"F1.wireOp",EDGE,"E22.14.12.0"),sQuery(id+"F1.wireOp",EDGE,"E22.18.12.0"),sQuery(id+"F1.wireOp",EDGE,"E22.22.12.0"),sQuery(id+"F1.wireOp",EDGE,"E22.26.12.0"),sQuery(id+"F1.wireOp",EDGE,"E22.29.12.0"),sQuery(id+"F1.wireOp",EDGE,"E22.3.13.0"),sQuery(id+"F1.wireOp",EDGE,"E22.7.13.0"),sQuery(id+"F1.wireOp",EDGE,"E22.10.13.0"),sQuery(id+"F1.wireOp",EDGE,"E22.14.13.0"),sQuery(id+"F1.wireOp",EDGE,"E22.18.13.0"),sQuery(id+"F1.wireOp",EDGE,"E22.22.13.0"),sQuery(id+"F1.wireOp",EDGE,"E22.26.13.0"),sQuery(id+"F1.wireOp",EDGE,"E22.29.13.0"),sQuery(id+"F1.wireOp",EDGE,"E22.3.14.0"),sQuery(id+"F1.wireOp",EDGE,"E22.7.14.0"),sQuery(id+"F1.wireOp",EDGE,"E22.10.14.0"),sQuery(id+"F1.wireOp",EDGE,"E22.14.14.0"),sQuery(id+"F1.wireOp",EDGE,"E22.18.14.0"),sQuery(id+"F1.wireOp",EDGE,"E22.22.14.0"),sQuery(id+"F1.wireOp",EDGE,"E22.26.14.0"),sQuery(id+"F1.wireOp",EDGE,"E22.29.14.0"),sQuery(id+"F1.wireOp",EDGE,"E22.3.15.0"),sQuery(id+"F1.wireOp",EDGE,"E22.7.15.0"),sQuery(id+"F1.wireOp",EDGE,"E22.10.15.0"),sQuery(id+"F1.wireOp",EDGE,"E22.14.15.0"),sQuery(id+"F1.wireOp",EDGE,"E22.18.15.0"),sQuery(id+"F1.wireOp",EDGE,"E22.22.15.0"),sQuery(id+"F1.wireOp",EDGE,"E22.26.15.0"),sQuery(id+"F1.wireOp",EDGE,"E22.29.15.0"),sQuery(id+"F1.wireOp",EDGE,"E22.3.16.0"),sQuery(id+"F1.wireOp",EDGE,"E22.7.16.0"),sQuery(id+"F1.wireOp",EDGE,"E22.10.16.0"),sQuery(id+"F1.wireOp",EDGE,"E22.14.16.0"),sQuery(id+"F1.wireOp",EDGE,"E22.18.16.0"),sQuery(id+"F1.wireOp",EDGE,"E22.22.16.0"),sQuery(id+"F1.wireOp",EDGE,"E22.26.16.0"),sQuery(id+"F1.wireOp",EDGE,"E22.29.16.0"),sQuery(id+"F1.wireOp",EDGE,"E22.3.17.0"),sQuery(id+"F1.wireOp",EDGE,"E22.7.17.0"),sQuery(id+"F1.wireOp",EDGE,"E22.10.17.0"),sQuery(id+"F1.wireOp",EDGE,"E22.14.17.0"),sQuery(id+"F1.wireOp",EDGE,"E22.18.17.0"),sQuery(id+"F1.wireOp",EDGE,"E22.22.17.0"),sQuery(id+"F1.wireOp",EDGE,"E22.26.17.0"),sQuery(id+"F1.wireOp",EDGE,"E22.29.17.0"),sQuery(id+"F1.wireOp",EDGE,"E22.3.18.0"),sQuery(id+"F1.wireOp",EDGE,"E22.7.18.0"),sQuery(id+"F1.wireOp",EDGE,"E22.10.18.0"),sQuery(id+"F1.wireOp",EDGE,"E22.14.18.0"),sQuery(id+"F1.wireOp",EDGE,"E22.18.18.0"),sQuery(id+"F1.wireOp",EDGE,"E22.22.18.0"),sQuery(id+"F1.wireOp",EDGE,"E22.26.18.0"),sQuery(id+"F1.wireOp",EDGE,"E22.29.18.0"),sQuery(id+"F1.wireOp",EDGE,"E22.3.19.0"),sQuery(id+"F1.wireOp",EDGE,"E22.7.19.0"),sQuery(id+"F1.wireOp",EDGE,"E22.10.19.0"),sQuery(id+"F1.wireOp",EDGE,"E22.14.19.0"),sQuery(id+"F1.wireOp",EDGE,"E22.18.19.0"),sQuery(id+"F1.wireOp",EDGE,"E22.22.19.0"),sQuery(id+"F1.wireOp",EDGE,"E22.26.19.0"),sQuery(id+"F1.wireOp",EDGE,"E22.29.19.0"),sQuery(id+"F1.wireOp",EDGE,"E22.3.20.0"),sQuery(id+"F1.wireOp",EDGE,"E22.7.20.0"),sQuery(id+"F1.wireOp",EDGE,"E22.10.20.0"),sQuery(id+"F1.wireOp",EDGE,"E22.14.20.0"),sQuery(id+"F1.wireOp",EDGE,"E22.18.20.0"),sQuery(id+"F1.wireOp",EDGE,"E22.22.20.0"),sQuery(id+"F1.wireOp",EDGE,"E22.26.20.0"),sQuery(id+"F1.wireOp",EDGE,"E22.29.20.0"),sQuery(id+"F1.wireOp",EDGE,"E22.3.21.0"),sQuery(id+"F1.wireOp",EDGE,"E22.7.21.0"),sQuery(id+"F1.wireOp",EDGE,"E22.10.21.0"),sQuery(id+"F1.wireOp",EDGE,"E22.14.21.0"),sQuery(id+"F1.wireOp",EDGE,"E22.18.21.0"),sQuery(id+"F1.wireOp",EDGE,"E22.22.21.0"),sQuery(id+"F1.wireOp",EDGE,"E22.26.21.0"),sQuery(id+"F1.wireOp",EDGE,"E22.29.21.0"),sQuery(id+"F1.wireOp",EDGE,"E22.3.22.0"),sQuery(id+"F1.wireOp",EDGE,"E22.7.22.0"),sQuery(id+"F1.wireOp",EDGE,"E22.10.22.0"),sQuery(id+"F1.wireOp",EDGE,"E22.14.22.0"),sQuery(id+"F1.wireOp",EDGE,"E22.18.22.0"),sQuery(id+"F1.wireOp",EDGE,"E22.22.22.0"),sQuery(id+"F1.wireOp",EDGE,"E22.26.22.0"),sQuery(id+"F1.wireOp",EDGE,"E22.29.22.0"),sQuery(id+"F1.wireOp",EDGE,"E22.3.23.0"),sQuery(id+"F1.wireOp",EDGE,"E22.7.23.0"),sQuery(id+"F1.wireOp",EDGE,"E22.10.23.0"),sQuery(id+"F1.wireOp",EDGE,"E22.14.23.0"),sQuery(id+"F1.wireOp",EDGE,"E22.18.23.0"),sQuery(id+"F1.wireOp",EDGE,"E22.22.23.0"),sQuery(id+"F1.wireOp",EDGE,"E22.26.23.0"),sQuery(id+"F1.wireOp",EDGE,"E22.29.23.0"),sQuery(id+"F1.wireOp",EDGE,"E22.3.24.0"),sQuery(id+"F1.wireOp",EDGE,"E22.7.24.0"),sQuery(id+"F1.wireOp",EDGE,"E22.10.24.0"),sQuery(id+"F1.wireOp",EDGE,"E22.14.24.0"),sQuery(id+"F1.wireOp",EDGE,"E22.18.24.0"),sQuery(id+"F1.wireOp",EDGE,"E22.22.24.0"),sQuery(id+"F1.wireOp",EDGE,"E22.26.24.0"),sQuery(id+"F1.wireOp",EDGE,"E22.29.24.0"),sQuery(id+"F1.wireOp",EDGE,"E22.3.25.0"),sQuery(id+"F1.wireOp",EDGE,"E22.7.25.0"),sQuery(id+"F1.wireOp",EDGE,"E22.10.25.0"),sQuery(id+"F1.wireOp",EDGE,"E22.14.25.0"),sQuery(id+"F1.wireOp",EDGE,"E22.18.25.0"),sQuery(id+"F1.wireOp",EDGE,"E22.22.25.0"),sQuery(id+"F1.wireOp",EDGE,"E22.26.25.0"),sQuery(id+"F1.wireOp",EDGE,"E22.29.25.0"),sQuery(id+"F1.wireOp",EDGE,"E22.3.26.0"),sQuery(id+"F1.wireOp",EDGE,"E22.7.26.0"),sQuery(id+"F1.wireOp",EDGE,"E22.10.26.0"),sQuery(id+"F1.wireOp",EDGE,"E22.14.26.0"),sQuery(id+"F1.wireOp",EDGE,"E22.18.26.0"),sQuery(id+"F1.wireOp",EDGE,"E22.22.26.0"),sQuery(id+"F1.wireOp",EDGE,"E22.26.26.0"),sQuery(id+"F1.wireOp",EDGE,"E22.29.26.0"),sQuery(id+"F1.wireOp",EDGE,"E22.3.27.0"),sQuery(id+"F1.wireOp",EDGE,"E22.7.27.0"),sQuery(id+"F1.wireOp",EDGE,"E22.10.27.0"),sQuery(id+"F1.wireOp",EDGE,"E22.14.27.0"),sQuery(id+"F1.wireOp",EDGE,"E22.18.27.0"),sQuery(id+"F1.wireOp",EDGE,"E22.22.27.0"),sQuery(id+"F1.wireOp",EDGE,"E22.26.27.0"),sQuery(id+"F1.wireOp",EDGE,"E22.29.27.0"),sQuery(id+"F1.wireOp",EDGE,"E22.3.28.0"),sQuery(id+"F1.wireOp",EDGE,"E22.7.28.0"),sQuery(id+"F1.wireOp",EDGE,"E22.10.28.0"),sQuery(id+"F1.wireOp",EDGE,"E22.14.28.0"),sQuery(id+"F1.wireOp",EDGE,"E22.18.28.0"),sQuery(id+"F1.wireOp",EDGE,"E22.22.28.0"),sQuery(id+"F1.wireOp",EDGE,"E22.26.28.0"),sQuery(id+"F1.wireOp",EDGE,"E22.29.28.0"),sQuery(id+"F1.wireOp",EDGE,"E22.3.29.0"),sQuery(id+"F1.wireOp",EDGE,"E22.7.29.0"),sQuery(id+"F1.wireOp",EDGE,"E22.10.29.0"),sQuery(id+"F1.wireOp",EDGE,"E22.14.29.0"),sQuery(id+"F1.wireOp",EDGE,"E22.18.29.0"),sQuery(id+"F1.wireOp",EDGE,"E22.22.29.0"),sQuery(id+"F1.wireOp",EDGE,"E22.26.29.0"),sQuery(id+"F1.wireOp",EDGE,"E22.29.29.0"),sQuery(id+"F1.wireOp",EDGE,"E23"),sQuery(id+"F1.wireOp",EDGE,"E24.trimOffspring"),sQuery(id+"F1.wireOp",EDGE,"E25.trimOffspring"),sQuery(id+"F1.wireOp",EDGE,"E26.trimOffspring"),sQuery(id+"F1.wireOp",EDGE,"E27.trimOffspring"),sQuery(id+"F1.wireOp",EDGE,"E28.trimOffspring"),sQuery(id+"F1.wireOp",EDGE,"E29.trimOffspring"),sQuery(id+"F1.wireOp",EDGE,"E30.trimOffspring"),sQuery(id+"F1.wireOp",EDGE,"E31.trimOffspring"),sQuery(id+"F1.wireOp",EDGE,"E32.trimOffspring"),sQuery(id+"F1.wireOp",EDGE,"E33.trimOffspring"),sQuery(id+"F1.wireOp",EDGE,"E34.trimOffspring"),sQuery(id+"F1.wireOp",EDGE,"E35.trimOffspring"),sQuery(id+"F1.wireOp",EDGE,"E36.trimOffspring"),sQuery(id+"F1.wireOp",EDGE,"E37.trimOffspring"),sQuery(id+"F1.wireOp",EDGE,"E38.trimOffspring"),sQuery(id+"F1.wireOp",EDGE,"E39.trimOffspring"),sQuery(id+"F1.wireOp",EDGE,"E40.trimOffspring"),sQuery(id+"F1.wireOp",EDGE,"E41.trimOffspring"),sQuery(id+"F1.wireOp",EDGE,"E42.trimOffspring"),sQuery(id+"F1.wireOp",EDGE,"E43.trimOffspring"),sQuery(id+"F1.wireOp",EDGE,"E44.trimOffspring"),sQuery(id+"F1.wireOp",EDGE,"E45.trimOffspring"),sQuery(id+"F1.wireOp",EDGE,"E46.trimOffspring"),sQuery(id+"F1.wireOp",EDGE,"E47.trimOffspring"),sQuery(id+"F1.wireOp",EDGE,"E48.trimOffspring"),sQuery(id+"F1.wireOp",EDGE,"E49.trimOffspring"),sQuery(id+"F1.wireOp",EDGE,"E50.trimOffspring"),sQuery(id+"F1.wireOp",EDGE,"E51.trimOffspring"),sQuery(id+"F1.wireOp",EDGE,"E52.trimOffspring")])],"isStart":true}),makeQuery(id+"F7.opExtrude","SWEPT_FACE",FACE,{"disambiguationData":[OSD([sQuery(id+"F6.wireOp",EDGE,"E58")])]})]});
            chamfer(context, id + "F8", {"entities" : qUnion([Q0]), "width" : 5 * mm, "tangentPropagation" : true});
        }
        {
            var Q0;
            Q0=makeQuery(id+"F4.boolean.opBoolean","INTERSECT",EDGE,{"derivedFrom":[makeQuery(id+"F2.opExtrude","SWEPT_FACE",FACE,{"disambiguationData":[OSD([sQuery(id+"F1.wireOp",EDGE,"E22.14.20.0"),sQuery(id+"F1.wireOp",EDGE,"E22.18.20.0")])]}),makeQuery(id+"F4.opRevolve","SWEPT_FACE",FACE,{"disambiguationData":[OSD([sQuery(id+"F3.wireOp",EDGE,"E53.top")])]})]});
            var Q1;
            Q1=makeQuery(id+"F4.boolean.opBoolean","INTERSECT",EDGE,{"derivedFrom":[makeQuery(id+"F2.opExtrude","SWEPT_FACE",FACE,{"disambiguationData":[OSD([sQuery(id+"F1.wireOp",EDGE,"E22.14.20.0"),sQuery(id+"F1.wireOp",EDGE,"E22.18.20.0")])]}),makeQuery(id+"F4.opRevolve","SWEPT_FACE",FACE,{"disambiguationData":[OSD([sQuery(id+"F3.wireOp",EDGE,"E53.bottom")])]})]});
            var Q2;
            Q2=makeQuery(id+"F4.boolean.opBoolean","INTERSECT",EDGE,{"derivedFrom":[makeQuery(id+"F2.opExtrude","SWEPT_FACE",FACE,{"disambiguationData":[OSD([sQuery(id+"F1.wireOp",EDGE,"E22.26.20.0")])]}),makeQuery(id+"F4.opRevolve","SWEPT_FACE",FACE,{"disambiguationData":[OSD([sQuery(id+"F3.wireOp",EDGE,"E53.top")])]})]});
            var Q3;
            Q3=makeQuery(id+"F4.boolean.opBoolean","INTERSECT",EDGE,{"derivedFrom":[makeQuery(id+"F2.opExtrude","SWEPT_FACE",FACE,{"disambiguationData":[OSD([sQuery(id+"F1.wireOp",EDGE,"E22.7.20.0")])]}),makeQuery(id+"F4.opRevolve","SWEPT_FACE",FACE,{"disambiguationData":[OSD([sQuery(id+"F3.wireOp",EDGE,"E53.top")])]})]});
            var Q4;
            Q4=makeQuery(id+"F4.boolean.opBoolean","INTERSECT",EDGE,{"derivedFrom":[makeQuery(id+"F2.opExtrude","SWEPT_FACE",FACE,{"disambiguationData":[OSD([sQuery(id+"F1.wireOp",EDGE,"E22.7.21.0")])]}),makeQuery(id+"F4.opRevolve","SWEPT_FACE",FACE,{"disambiguationData":[OSD([sQuery(id+"F3.wireOp",EDGE,"E53.top")])]})]});
            var Q5;
            Q5=makeQuery(id+"F4.boolean.opBoolean","INTERSECT",EDGE,{"derivedFrom":[makeQuery(id+"F2.opExtrude","SWEPT_FACE",FACE,{"disambiguationData":[OSD([sQuery(id+"F1.wireOp",EDGE,"E22.7.22.0")])]}),makeQuery(id+"F4.opRevolve","SWEPT_FACE",FACE,{"disambiguationData":[OSD([sQuery(id+"F3.wireOp",EDGE,"E53.top")])]})]});
            var Q6;
            Q6=makeQuery(id+"F4.boolean.opBoolean","INTERSECT",EDGE,{"derivedFrom":[makeQuery(id+"F2.opExtrude","SWEPT_FACE",FACE,{"disambiguationData":[OSD([sQuery(id+"F1.wireOp",EDGE,"E22.7.23.0")])]}),makeQuery(id+"F4.opRevolve","SWEPT_FACE",FACE,{"disambiguationData":[OSD([sQuery(id+"F3.wireOp",EDGE,"E53.top")])]})]});
            var Q7;
            Q7=makeQuery(id+"F4.boolean.opBoolean","INTERSECT",EDGE,{"derivedFrom":[makeQuery(id+"F2.opExtrude","SWEPT_FACE",FACE,{"disambiguationData":[OSD([sQuery(id+"F1.wireOp",EDGE,"E22.7.24.0")])]}),makeQuery(id+"F4.opRevolve","SWEPT_FACE",FACE,{"disambiguationData":[OSD([sQuery(id+"F3.wireOp",EDGE,"E53.top")])]})]});
            var Q8;
            Q8=makeQuery(id+"F4.boolean.opBoolean","INTERSECT",EDGE,{"derivedFrom":[makeQuery(id+"F2.opExtrude","SWEPT_FACE",FACE,{"disambiguationData":[OSD([sQuery(id+"F1.wireOp",EDGE,"E22.7.25.0")])]}),makeQuery(id+"F4.opRevolve","SWEPT_FACE",FACE,{"disambiguationData":[OSD([sQuery(id+"F3.wireOp",EDGE,"E53.top")])]})]});
            var Q9;
            Q9=makeQuery(id+"F4.boolean.opBoolean","INTERSECT",EDGE,{"derivedFrom":[makeQuery(id+"F2.opExtrude","SWEPT_FACE",FACE,{"disambiguationData":[OSD([sQuery(id+"F1.wireOp",EDGE,"E22.7.26.0")])]}),makeQuery(id+"F4.opRevolve","SWEPT_FACE",FACE,{"disambiguationData":[OSD([sQuery(id+"F3.wireOp",EDGE,"E53.top")])]})]});
            var Q10;
            Q10=makeQuery(id+"F4.boolean.opBoolean","INTERSECT",EDGE,{"derivedFrom":[makeQuery(id+"F2.opExtrude","SWEPT_FACE",FACE,{"disambiguationData":[OSD([sQuery(id+"F1.wireOp",EDGE,"E22.7.27.0")])]}),makeQuery(id+"F4.opRevolve","SWEPT_FACE",FACE,{"disambiguationData":[OSD([sQuery(id+"F3.wireOp",EDGE,"E53.top")])]})]});
            var Q11;
            Q11=makeQuery(id+"F4.boolean.opBoolean","INTERSECT",EDGE,{"derivedFrom":[makeQuery(id+"F2.opExtrude","SWEPT_FACE",FACE,{"disambiguationData":[OSD([sQuery(id+"F1.wireOp",EDGE,"E22.7.28.0")])]}),makeQuery(id+"F4.opRevolve","SWEPT_FACE",FACE,{"disambiguationData":[OSD([sQuery(id+"F3.wireOp",EDGE,"E53.top")])]})]});
            var Q12;
            Q12=makeQuery(id+"F4.boolean.opBoolean","INTERSECT",EDGE,{"derivedFrom":[makeQuery(id+"F2.opExtrude","SWEPT_FACE",FACE,{"disambiguationData":[OSD([sQuery(id+"F1.wireOp",EDGE,"E22.7.29.0")])]}),makeQuery(id+"F4.opRevolve","SWEPT_FACE",FACE,{"disambiguationData":[OSD([sQuery(id+"F3.wireOp",EDGE,"E53.top")])]})]});
            var Q13;
            Q13=makeQuery(id+"F4.boolean.opBoolean","INTERSECT",EDGE,{"derivedFrom":[makeQuery(id+"F2.opExtrude","SWEPT_FACE",FACE,{"disambiguationData":[OSD([sQuery(id+"F1.wireOp",EDGE,"E15.0")])]}),makeQuery(id+"F4.opRevolve","SWEPT_FACE",FACE,{"disambiguationData":[OSD([sQuery(id+"F3.wireOp",EDGE,"E53.top")])]})]});
            var Q14;
            Q14=makeQuery(id+"F4.boolean.opBoolean","INTERSECT",EDGE,{"derivedFrom":[makeQuery(id+"F2.opExtrude","SWEPT_FACE",FACE,{"disambiguationData":[OSD([sQuery(id+"F1.wireOp",EDGE,"E20.1.2")])]}),makeQuery(id+"F4.opRevolve","SWEPT_FACE",FACE,{"disambiguationData":[OSD([sQuery(id+"F3.wireOp",EDGE,"E53.top")])]})]});
            var Q15;
            Q15=makeQuery(id+"F4.boolean.opBoolean","INTERSECT",EDGE,{"derivedFrom":[makeQuery(id+"F2.opExtrude","SWEPT_FACE",FACE,{"disambiguationData":[OSD([sQuery(id+"F1.wireOp",EDGE,"E20.2.2")])]}),makeQuery(id+"F4.opRevolve","SWEPT_FACE",FACE,{"disambiguationData":[OSD([sQuery(id+"F3.wireOp",EDGE,"E53.top")])]})]});
            var Q16;
            Q16=makeQuery(id+"F4.boolean.opBoolean","INTERSECT",EDGE,{"derivedFrom":[makeQuery(id+"F2.opExtrude","SWEPT_FACE",FACE,{"disambiguationData":[OSD([sQuery(id+"F1.wireOp",EDGE,"E21.7.3.0")])]}),makeQuery(id+"F4.opRevolve","SWEPT_FACE",FACE,{"disambiguationData":[OSD([sQuery(id+"F3.wireOp",EDGE,"E53.top")])]})]});
            var Q17;
            Q17=makeQuery(id+"F4.boolean.opBoolean","INTERSECT",EDGE,{"derivedFrom":[makeQuery(id+"F2.opExtrude","SWEPT_FACE",FACE,{"disambiguationData":[OSD([sQuery(id+"F1.wireOp",EDGE,"E21.7.4.0")])]}),makeQuery(id+"F4.opRevolve","SWEPT_FACE",FACE,{"disambiguationData":[OSD([sQuery(id+"F3.wireOp",EDGE,"E53.top")])]})]});
            var Q18;
            Q18=makeQuery(id+"F4.boolean.opBoolean","INTERSECT",EDGE,{"derivedFrom":[makeQuery(id+"F2.opExtrude","SWEPT_FACE",FACE,{"disambiguationData":[OSD([sQuery(id+"F1.wireOp",EDGE,"E21.7.5.0")])]}),makeQuery(id+"F4.opRevolve","SWEPT_FACE",FACE,{"disambiguationData":[OSD([sQuery(id+"F3.wireOp",EDGE,"E53.top")])]})]});
            var Q19;
            Q19=makeQuery(id+"F4.boolean.opBoolean","INTERSECT",EDGE,{"derivedFrom":[makeQuery(id+"F2.opExtrude","SWEPT_FACE",FACE,{"disambiguationData":[OSD([sQuery(id+"F1.wireOp",EDGE,"E22.7.6.0")])]}),makeQuery(id+"F4.opRevolve","SWEPT_FACE",FACE,{"disambiguationData":[OSD([sQuery(id+"F3.wireOp",EDGE,"E53.top")])]})]});
            var Q20;
            Q20=makeQuery(id+"F4.boolean.opBoolean","INTERSECT",EDGE,{"derivedFrom":[makeQuery(id+"F2.opExtrude","SWEPT_FACE",FACE,{"disambiguationData":[OSD([sQuery(id+"F1.wireOp",EDGE,"E22.7.7.0")])]}),makeQuery(id+"F4.opRevolve","SWEPT_FACE",FACE,{"disambiguationData":[OSD([sQuery(id+"F3.wireOp",EDGE,"E53.top")])]})]});
            var Q21;
            Q21=makeQuery(id+"F4.boolean.opBoolean","INTERSECT",EDGE,{"derivedFrom":[makeQuery(id+"F2.opExtrude","SWEPT_FACE",FACE,{"disambiguationData":[OSD([sQuery(id+"F1.wireOp",EDGE,"E22.7.8.0")])]}),makeQuery(id+"F4.opRevolve","SWEPT_FACE",FACE,{"disambiguationData":[OSD([sQuery(id+"F3.wireOp",EDGE,"E53.top")])]})]});
            var Q22;
            Q22=makeQuery(id+"F4.boolean.opBoolean","INTERSECT",EDGE,{"derivedFrom":[makeQuery(id+"F2.opExtrude","SWEPT_FACE",FACE,{"disambiguationData":[OSD([sQuery(id+"F1.wireOp",EDGE,"E22.7.9.0")])]}),makeQuery(id+"F4.opRevolve","SWEPT_FACE",FACE,{"disambiguationData":[OSD([sQuery(id+"F3.wireOp",EDGE,"E53.top")])]})]});
            var Q23;
            Q23=makeQuery(id+"F4.boolean.opBoolean","INTERSECT",EDGE,{"derivedFrom":[makeQuery(id+"F2.opExtrude","SWEPT_FACE",FACE,{"disambiguationData":[OSD([sQuery(id+"F1.wireOp",EDGE,"E22.7.10.0")])]}),makeQuery(id+"F4.opRevolve","SWEPT_FACE",FACE,{"disambiguationData":[OSD([sQuery(id+"F3.wireOp",EDGE,"E53.top")])]})]});
            var Q24;
            Q24=makeQuery(id+"F4.boolean.opBoolean","INTERSECT",EDGE,{"derivedFrom":[makeQuery(id+"F2.opExtrude","SWEPT_FACE",FACE,{"disambiguationData":[OSD([sQuery(id+"F1.wireOp",EDGE,"E22.7.11.0")])]}),makeQuery(id+"F4.opRevolve","SWEPT_FACE",FACE,{"disambiguationData":[OSD([sQuery(id+"F3.wireOp",EDGE,"E53.top")])]})]});
            var Q25;
            Q25=makeQuery(id+"F4.boolean.opBoolean","INTERSECT",EDGE,{"derivedFrom":[makeQuery(id+"F2.opExtrude","SWEPT_FACE",FACE,{"disambiguationData":[OSD([sQuery(id+"F1.wireOp",EDGE,"E22.7.12.0")])]}),makeQuery(id+"F4.opRevolve","SWEPT_FACE",FACE,{"disambiguationData":[OSD([sQuery(id+"F3.wireOp",EDGE,"E53.top")])]})]});
            var Q26;
            Q26=makeQuery(id+"F4.boolean.opBoolean","INTERSECT",EDGE,{"derivedFrom":[makeQuery(id+"F2.opExtrude","SWEPT_FACE",FACE,{"disambiguationData":[OSD([sQuery(id+"F1.wireOp",EDGE,"E22.7.13.0")])]}),makeQuery(id+"F4.opRevolve","SWEPT_FACE",FACE,{"disambiguationData":[OSD([sQuery(id+"F3.wireOp",EDGE,"E53.top")])]})]});
            var Q27;
            Q27=makeQuery(id+"F4.boolean.opBoolean","INTERSECT",EDGE,{"derivedFrom":[makeQuery(id+"F2.opExtrude","SWEPT_FACE",FACE,{"disambiguationData":[OSD([sQuery(id+"F1.wireOp",EDGE,"E22.7.14.0")])]}),makeQuery(id+"F4.opRevolve","SWEPT_FACE",FACE,{"disambiguationData":[OSD([sQuery(id+"F3.wireOp",EDGE,"E53.top")])]})]});
            var Q28;
            Q28=makeQuery(id+"F4.boolean.opBoolean","INTERSECT",EDGE,{"derivedFrom":[makeQuery(id+"F2.opExtrude","SWEPT_FACE",FACE,{"disambiguationData":[OSD([sQuery(id+"F1.wireOp",EDGE,"E22.7.15.0")])]}),makeQuery(id+"F4.opRevolve","SWEPT_FACE",FACE,{"disambiguationData":[OSD([sQuery(id+"F3.wireOp",EDGE,"E53.top")])]})]});
            var Q29;
            Q29=makeQuery(id+"F4.boolean.opBoolean","INTERSECT",EDGE,{"derivedFrom":[makeQuery(id+"F2.opExtrude","SWEPT_FACE",FACE,{"disambiguationData":[OSD([sQuery(id+"F1.wireOp",EDGE,"E22.7.16.0")])]}),makeQuery(id+"F4.opRevolve","SWEPT_FACE",FACE,{"disambiguationData":[OSD([sQuery(id+"F3.wireOp",EDGE,"E53.top")])]})]});
            var Q30;
            Q30=makeQuery(id+"F4.boolean.opBoolean","INTERSECT",EDGE,{"derivedFrom":[makeQuery(id+"F2.opExtrude","SWEPT_FACE",FACE,{"disambiguationData":[OSD([sQuery(id+"F1.wireOp",EDGE,"E22.7.17.0")])]}),makeQuery(id+"F4.opRevolve","SWEPT_FACE",FACE,{"disambiguationData":[OSD([sQuery(id+"F3.wireOp",EDGE,"E53.top")])]})]});
            var Q31;
            Q31=makeQuery(id+"F4.boolean.opBoolean","INTERSECT",EDGE,{"derivedFrom":[makeQuery(id+"F2.opExtrude","SWEPT_FACE",FACE,{"disambiguationData":[OSD([sQuery(id+"F1.wireOp",EDGE,"E22.7.18.0")])]}),makeQuery(id+"F4.opRevolve","SWEPT_FACE",FACE,{"disambiguationData":[OSD([sQuery(id+"F3.wireOp",EDGE,"E53.top")])]})]});
            var Q32;
            Q32=makeQuery(id+"F4.boolean.opBoolean","INTERSECT",EDGE,{"derivedFrom":[makeQuery(id+"F2.opExtrude","SWEPT_FACE",FACE,{"disambiguationData":[OSD([sQuery(id+"F1.wireOp",EDGE,"E22.7.19.0")])]}),makeQuery(id+"F4.opRevolve","SWEPT_FACE",FACE,{"disambiguationData":[OSD([sQuery(id+"F3.wireOp",EDGE,"E53.top")])]})]});
            var Q33;
            Q33=makeQuery(id+"F4.boolean.opBoolean","INTERSECT",EDGE,{"derivedFrom":[makeQuery(id+"F2.opExtrude","SWEPT_FACE",FACE,{"disambiguationData":[OSD([sQuery(id+"F1.wireOp",EDGE,"E22.26.21.0")])]}),makeQuery(id+"F4.opRevolve","SWEPT_FACE",FACE,{"disambiguationData":[OSD([sQuery(id+"F3.wireOp",EDGE,"E53.top")])]})]});
            var Q34;
            Q34=makeQuery(id+"F4.boolean.opBoolean","INTERSECT",EDGE,{"derivedFrom":[makeQuery(id+"F2.opExtrude","SWEPT_FACE",FACE,{"disambiguationData":[OSD([sQuery(id+"F1.wireOp",EDGE,"E22.14.21.0"),sQuery(id+"F1.wireOp",EDGE,"E22.18.21.0")])]}),makeQuery(id+"F4.opRevolve","SWEPT_FACE",FACE,{"disambiguationData":[OSD([sQuery(id+"F3.wireOp",EDGE,"E53.top")])]})]});
            var Q35;
            Q35=makeQuery(id+"F4.boolean.opBoolean","INTERSECT",EDGE,{"derivedFrom":[makeQuery(id+"F2.opExtrude","SWEPT_FACE",FACE,{"disambiguationData":[OSD([sQuery(id+"F1.wireOp",EDGE,"E22.14.21.0"),sQuery(id+"F1.wireOp",EDGE,"E22.18.21.0")])]}),makeQuery(id+"F4.opRevolve","SWEPT_FACE",FACE,{"disambiguationData":[OSD([sQuery(id+"F3.wireOp",EDGE,"E53.bottom")])]})]});
            var Q36;
            Q36=makeQuery(id+"F4.boolean.opBoolean","INTERSECT",EDGE,{"derivedFrom":[makeQuery(id+"F2.opExtrude","SWEPT_FACE",FACE,{"disambiguationData":[OSD([sQuery(id+"F1.wireOp",EDGE,"E22.26.22.0")])]}),makeQuery(id+"F4.opRevolve","SWEPT_FACE",FACE,{"disambiguationData":[OSD([sQuery(id+"F3.wireOp",EDGE,"E53.top")])]})]});
            var Q37;
            Q37=makeQuery(id+"F4.boolean.opBoolean","INTERSECT",EDGE,{"derivedFrom":[makeQuery(id+"F2.opExtrude","SWEPT_FACE",FACE,{"disambiguationData":[OSD([sQuery(id+"F1.wireOp",EDGE,"E22.14.22.0"),sQuery(id+"F1.wireOp",EDGE,"E22.18.22.0")])]}),makeQuery(id+"F4.opRevolve","SWEPT_FACE",FACE,{"disambiguationData":[OSD([sQuery(id+"F3.wireOp",EDGE,"E53.top")])]})]});
            var Q38;
            Q38=makeQuery(id+"F4.boolean.opBoolean","INTERSECT",EDGE,{"derivedFrom":[makeQuery(id+"F2.opExtrude","SWEPT_FACE",FACE,{"disambiguationData":[OSD([sQuery(id+"F1.wireOp",EDGE,"E22.14.22.0"),sQuery(id+"F1.wireOp",EDGE,"E22.18.22.0")])]}),makeQuery(id+"F4.opRevolve","SWEPT_FACE",FACE,{"disambiguationData":[OSD([sQuery(id+"F3.wireOp",EDGE,"E53.bottom")])]})]});
            var Q39;
            Q39=makeQuery(id+"F4.boolean.opBoolean","INTERSECT",EDGE,{"derivedFrom":[makeQuery(id+"F2.opExtrude","SWEPT_FACE",FACE,{"disambiguationData":[OSD([sQuery(id+"F1.wireOp",EDGE,"E22.26.23.0")])]}),makeQuery(id+"F4.opRevolve","SWEPT_FACE",FACE,{"disambiguationData":[OSD([sQuery(id+"F3.wireOp",EDGE,"E53.top")])]})]});
            var Q40;
            Q40=makeQuery(id+"F4.boolean.opBoolean","INTERSECT",EDGE,{"derivedFrom":[makeQuery(id+"F2.opExtrude","SWEPT_FACE",FACE,{"disambiguationData":[OSD([sQuery(id+"F1.wireOp",EDGE,"E22.14.23.0"),sQuery(id+"F1.wireOp",EDGE,"E22.18.23.0")])]}),makeQuery(id+"F4.opRevolve","SWEPT_FACE",FACE,{"disambiguationData":[OSD([sQuery(id+"F3.wireOp",EDGE,"E53.top")])]})]});
            var Q41;
            Q41=makeQuery(id+"F4.boolean.opBoolean","INTERSECT",EDGE,{"derivedFrom":[makeQuery(id+"F2.opExtrude","SWEPT_FACE",FACE,{"disambiguationData":[OSD([sQuery(id+"F1.wireOp",EDGE,"E22.26.23.0")])]}),makeQuery(id+"F4.opRevolve","SWEPT_FACE",FACE,{"disambiguationData":[OSD([sQuery(id+"F3.wireOp",EDGE,"E53.bottom")])]})]});
            var Q42;
            Q42=makeQuery(id+"F4.boolean.opBoolean","INTERSECT",EDGE,{"derivedFrom":[makeQuery(id+"F2.opExtrude","SWEPT_FACE",FACE,{"disambiguationData":[OSD([sQuery(id+"F1.wireOp",EDGE,"E22.14.23.0"),sQuery(id+"F1.wireOp",EDGE,"E22.18.23.0")])]}),makeQuery(id+"F4.opRevolve","SWEPT_FACE",FACE,{"disambiguationData":[OSD([sQuery(id+"F3.wireOp",EDGE,"E53.bottom")])]})]});
            var Q43;
            Q43=makeQuery(id+"F4.boolean.opBoolean","INTERSECT",EDGE,{"derivedFrom":[makeQuery(id+"F2.opExtrude","SWEPT_FACE",FACE,{"disambiguationData":[OSD([sQuery(id+"F1.wireOp",EDGE,"E22.26.24.0")])]}),makeQuery(id+"F4.opRevolve","SWEPT_FACE",FACE,{"disambiguationData":[OSD([sQuery(id+"F3.wireOp",EDGE,"E53.bottom")])]})]});
            var Q44;
            Q44=makeQuery(id+"F4.boolean.opBoolean","INTERSECT",EDGE,{"derivedFrom":[makeQuery(id+"F2.opExtrude","SWEPT_FACE",FACE,{"disambiguationData":[OSD([sQuery(id+"F1.wireOp",EDGE,"E22.26.24.0")])]}),makeQuery(id+"F4.opRevolve","SWEPT_FACE",FACE,{"disambiguationData":[OSD([sQuery(id+"F3.wireOp",EDGE,"E53.top")])]})]});
            var Q45;
            Q45=makeQuery(id+"F4.boolean.opBoolean","INTERSECT",EDGE,{"derivedFrom":[makeQuery(id+"F2.opExtrude","SWEPT_FACE",FACE,{"disambiguationData":[OSD([sQuery(id+"F1.wireOp",EDGE,"E22.14.24.0"),sQuery(id+"F1.wireOp",EDGE,"E22.18.24.0")])]}),makeQuery(id+"F4.opRevolve","SWEPT_FACE",FACE,{"disambiguationData":[OSD([sQuery(id+"F3.wireOp",EDGE,"E53.top")])]})]});
            var Q46;
            Q46=makeQuery(id+"F4.boolean.opBoolean","INTERSECT",EDGE,{"derivedFrom":[makeQuery(id+"F2.opExtrude","SWEPT_FACE",FACE,{"disambiguationData":[OSD([sQuery(id+"F1.wireOp",EDGE,"E22.14.24.0"),sQuery(id+"F1.wireOp",EDGE,"E22.18.24.0")])]}),makeQuery(id+"F4.opRevolve","SWEPT_FACE",FACE,{"disambiguationData":[OSD([sQuery(id+"F3.wireOp",EDGE,"E53.bottom")])]})]});
            var Q47;
            Q47=makeQuery(id+"F4.boolean.opBoolean","INTERSECT",EDGE,{"derivedFrom":[makeQuery(id+"F2.opExtrude","SWEPT_FACE",FACE,{"disambiguationData":[OSD([sQuery(id+"F1.wireOp",EDGE,"E22.26.25.0")])]}),makeQuery(id+"F4.opRevolve","SWEPT_FACE",FACE,{"disambiguationData":[OSD([sQuery(id+"F3.wireOp",EDGE,"E53.top")])]})]});
            var Q48;
            Q48=makeQuery(id+"F4.boolean.opBoolean","INTERSECT",EDGE,{"derivedFrom":[makeQuery(id+"F2.opExtrude","SWEPT_FACE",FACE,{"disambiguationData":[OSD([sQuery(id+"F1.wireOp",EDGE,"E22.26.25.0")])]}),makeQuery(id+"F4.opRevolve","SWEPT_FACE",FACE,{"disambiguationData":[OSD([sQuery(id+"F3.wireOp",EDGE,"E53.bottom")])]})]});
            var Q49;
            Q49=makeQuery(id+"F4.boolean.opBoolean","INTERSECT",EDGE,{"derivedFrom":[makeQuery(id+"F2.opExtrude","SWEPT_FACE",FACE,{"disambiguationData":[OSD([sQuery(id+"F1.wireOp",EDGE,"E22.14.25.0"),sQuery(id+"F1.wireOp",EDGE,"E22.18.25.0")])]}),makeQuery(id+"F4.opRevolve","SWEPT_FACE",FACE,{"disambiguationData":[OSD([sQuery(id+"F3.wireOp",EDGE,"E53.top")])]})]});
            var Q50;
            Q50=makeQuery(id+"F4.boolean.opBoolean","INTERSECT",EDGE,{"derivedFrom":[makeQuery(id+"F2.opExtrude","SWEPT_FACE",FACE,{"disambiguationData":[OSD([sQuery(id+"F1.wireOp",EDGE,"E22.14.25.0"),sQuery(id+"F1.wireOp",EDGE,"E22.18.25.0")])]}),makeQuery(id+"F4.opRevolve","SWEPT_FACE",FACE,{"disambiguationData":[OSD([sQuery(id+"F3.wireOp",EDGE,"E53.bottom")])]})]});
            var Q51;
            Q51=makeQuery(id+"F4.boolean.opBoolean","INTERSECT",EDGE,{"derivedFrom":[makeQuery(id+"F2.opExtrude","SWEPT_FACE",FACE,{"disambiguationData":[OSD([sQuery(id+"F1.wireOp",EDGE,"E22.26.26.0")])]}),makeQuery(id+"F4.opRevolve","SWEPT_FACE",FACE,{"disambiguationData":[OSD([sQuery(id+"F3.wireOp",EDGE,"E53.top")])]})]});
            var Q52;
            Q52=makeQuery(id+"F4.boolean.opBoolean","INTERSECT",EDGE,{"derivedFrom":[makeQuery(id+"F2.opExtrude","SWEPT_FACE",FACE,{"disambiguationData":[OSD([sQuery(id+"F1.wireOp",EDGE,"E22.26.26.0")])]}),makeQuery(id+"F4.opRevolve","SWEPT_FACE",FACE,{"disambiguationData":[OSD([sQuery(id+"F3.wireOp",EDGE,"E53.bottom")])]})]});
            var Q53;
            Q53=makeQuery(id+"F4.boolean.opBoolean","INTERSECT",EDGE,{"derivedFrom":[makeQuery(id+"F2.opExtrude","SWEPT_FACE",FACE,{"disambiguationData":[OSD([sQuery(id+"F1.wireOp",EDGE,"E22.14.26.0"),sQuery(id+"F1.wireOp",EDGE,"E22.18.26.0")])]}),makeQuery(id+"F4.opRevolve","SWEPT_FACE",FACE,{"disambiguationData":[OSD([sQuery(id+"F3.wireOp",EDGE,"E53.bottom")])]})]});
            var Q54;
            Q54=makeQuery(id+"F4.boolean.opBoolean","INTERSECT",EDGE,{"derivedFrom":[makeQuery(id+"F2.opExtrude","SWEPT_FACE",FACE,{"disambiguationData":[OSD([sQuery(id+"F1.wireOp",EDGE,"E22.14.26.0"),sQuery(id+"F1.wireOp",EDGE,"E22.18.26.0")])]}),makeQuery(id+"F4.opRevolve","SWEPT_FACE",FACE,{"disambiguationData":[OSD([sQuery(id+"F3.wireOp",EDGE,"E53.top")])]})]});
            var Q55;
            Q55=makeQuery(id+"F4.boolean.opBoolean","INTERSECT",EDGE,{"derivedFrom":[makeQuery(id+"F2.opExtrude","SWEPT_FACE",FACE,{"disambiguationData":[OSD([sQuery(id+"F1.wireOp",EDGE,"E22.26.27.0")])]}),makeQuery(id+"F4.opRevolve","SWEPT_FACE",FACE,{"disambiguationData":[OSD([sQuery(id+"F3.wireOp",EDGE,"E53.top")])]})]});
            var Q56;
            Q56=makeQuery(id+"F4.boolean.opBoolean","INTERSECT",EDGE,{"derivedFrom":[makeQuery(id+"F2.opExtrude","SWEPT_FACE",FACE,{"disambiguationData":[OSD([sQuery(id+"F1.wireOp",EDGE,"E22.26.27.0")])]}),makeQuery(id+"F4.opRevolve","SWEPT_FACE",FACE,{"disambiguationData":[OSD([sQuery(id+"F3.wireOp",EDGE,"E53.bottom")])]})]});
            var Q57;
            Q57=makeQuery(id+"F4.boolean.opBoolean","INTERSECT",EDGE,{"derivedFrom":[makeQuery(id+"F2.opExtrude","SWEPT_FACE",FACE,{"disambiguationData":[OSD([sQuery(id+"F1.wireOp",EDGE,"E22.14.27.0"),sQuery(id+"F1.wireOp",EDGE,"E22.18.27.0")])]}),makeQuery(id+"F4.opRevolve","SWEPT_FACE",FACE,{"disambiguationData":[OSD([sQuery(id+"F3.wireOp",EDGE,"E53.bottom")])]})]});
            var Q58;
            Q58=makeQuery(id+"F4.boolean.opBoolean","INTERSECT",EDGE,{"derivedFrom":[makeQuery(id+"F2.opExtrude","SWEPT_FACE",FACE,{"disambiguationData":[OSD([sQuery(id+"F1.wireOp",EDGE,"E22.14.27.0"),sQuery(id+"F1.wireOp",EDGE,"E22.18.27.0")])]}),makeQuery(id+"F4.opRevolve","SWEPT_FACE",FACE,{"disambiguationData":[OSD([sQuery(id+"F3.wireOp",EDGE,"E53.top")])]})]});
            var Q59;
            Q59=makeQuery(id+"F4.boolean.opBoolean","INTERSECT",EDGE,{"derivedFrom":[makeQuery(id+"F2.opExtrude","SWEPT_FACE",FACE,{"disambiguationData":[OSD([sQuery(id+"F1.wireOp",EDGE,"E22.26.28.0")])]}),makeQuery(id+"F4.opRevolve","SWEPT_FACE",FACE,{"disambiguationData":[OSD([sQuery(id+"F3.wireOp",EDGE,"E53.top")])]})]});
            var Q60;
            Q60=makeQuery(id+"F4.boolean.opBoolean","INTERSECT",EDGE,{"derivedFrom":[makeQuery(id+"F2.opExtrude","SWEPT_FACE",FACE,{"disambiguationData":[OSD([sQuery(id+"F1.wireOp",EDGE,"E22.14.28.0"),sQuery(id+"F1.wireOp",EDGE,"E22.18.28.0")])]}),makeQuery(id+"F4.opRevolve","SWEPT_FACE",FACE,{"disambiguationData":[OSD([sQuery(id+"F3.wireOp",EDGE,"E53.bottom")])]})]});
            var Q61;
            Q61=makeQuery(id+"F4.boolean.opBoolean","INTERSECT",EDGE,{"derivedFrom":[makeQuery(id+"F2.opExtrude","SWEPT_FACE",FACE,{"disambiguationData":[OSD([sQuery(id+"F1.wireOp",EDGE,"E22.14.28.0"),sQuery(id+"F1.wireOp",EDGE,"E22.18.28.0")])]}),makeQuery(id+"F4.opRevolve","SWEPT_FACE",FACE,{"disambiguationData":[OSD([sQuery(id+"F3.wireOp",EDGE,"E53.top")])]})]});
            var Q62;
            Q62=makeQuery(id+"F4.boolean.opBoolean","INTERSECT",EDGE,{"derivedFrom":[makeQuery(id+"F2.opExtrude","SWEPT_FACE",FACE,{"disambiguationData":[OSD([sQuery(id+"F1.wireOp",EDGE,"E22.26.29.0")])]}),makeQuery(id+"F4.opRevolve","SWEPT_FACE",FACE,{"disambiguationData":[OSD([sQuery(id+"F3.wireOp",EDGE,"E53.top")])]})]});
            var Q63;
            Q63=makeQuery(id+"F4.boolean.opBoolean","INTERSECT",EDGE,{"derivedFrom":[makeQuery(id+"F2.opExtrude","SWEPT_FACE",FACE,{"disambiguationData":[OSD([sQuery(id+"F1.wireOp",EDGE,"E22.26.29.0")])]}),makeQuery(id+"F4.opRevolve","SWEPT_FACE",FACE,{"disambiguationData":[OSD([sQuery(id+"F3.wireOp",EDGE,"E53.bottom")])]})]});
            var Q64;
            Q64=makeQuery(id+"F4.boolean.opBoolean","INTERSECT",EDGE,{"derivedFrom":[makeQuery(id+"F2.opExtrude","SWEPT_FACE",FACE,{"disambiguationData":[OSD([sQuery(id+"F1.wireOp",EDGE,"E22.14.29.0"),sQuery(id+"F1.wireOp",EDGE,"E22.18.29.0")])]}),makeQuery(id+"F4.opRevolve","SWEPT_FACE",FACE,{"disambiguationData":[OSD([sQuery(id+"F3.wireOp",EDGE,"E53.bottom")])]})]});
            var Q65;
            Q65=makeQuery(id+"F4.boolean.opBoolean","INTERSECT",EDGE,{"derivedFrom":[makeQuery(id+"F2.opExtrude","SWEPT_FACE",FACE,{"disambiguationData":[OSD([sQuery(id+"F1.wireOp",EDGE,"E22.14.29.0"),sQuery(id+"F1.wireOp",EDGE,"E22.18.29.0")])]}),makeQuery(id+"F4.opRevolve","SWEPT_FACE",FACE,{"disambiguationData":[OSD([sQuery(id+"F3.wireOp",EDGE,"E53.top")])]})]});
            var Q66;
            Q66=makeQuery(id+"F4.boolean.opBoolean","INTERSECT",EDGE,{"derivedFrom":[makeQuery(id+"F2.opExtrude","SWEPT_FACE",FACE,{"disambiguationData":[OSD([sQuery(id+"F1.wireOp",EDGE,"E18.MirrorCS")])]}),makeQuery(id+"F4.opRevolve","SWEPT_FACE",FACE,{"disambiguationData":[OSD([sQuery(id+"F3.wireOp",EDGE,"E53.top")])]})]});
            var Q67;
            Q67=makeQuery(id+"F4.boolean.opBoolean","INTERSECT",EDGE,{"derivedFrom":[makeQuery(id+"F2.opExtrude","SWEPT_FACE",FACE,{"disambiguationData":[OSD([sQuery(id+"F1.wireOp",EDGE,"E18.MirrorCS")])]}),makeQuery(id+"F4.opRevolve","SWEPT_FACE",FACE,{"disambiguationData":[OSD([sQuery(id+"F3.wireOp",EDGE,"E53.bottom")])]})]});
            var Q68;
            Q68=makeQuery(id+"F4.boolean.opBoolean","INTERSECT",EDGE,{"derivedFrom":[makeQuery(id+"F2.opExtrude","SWEPT_FACE",FACE,{"disambiguationData":[OSD([sQuery(id+"F1.wireOp",EDGE,"E13.0"),sQuery(id+"F1.wireOp",EDGE,"E16.MirrorCS")])]}),makeQuery(id+"F4.opRevolve","SWEPT_FACE",FACE,{"disambiguationData":[OSD([sQuery(id+"F3.wireOp",EDGE,"E53.bottom")])]})]});
            var Q69;
            Q69=makeQuery(id+"F4.boolean.opBoolean","INTERSECT",EDGE,{"derivedFrom":[makeQuery(id+"F2.opExtrude","SWEPT_FACE",FACE,{"disambiguationData":[OSD([sQuery(id+"F1.wireOp",EDGE,"E13.0"),sQuery(id+"F1.wireOp",EDGE,"E16.MirrorCS")])]}),makeQuery(id+"F4.opRevolve","SWEPT_FACE",FACE,{"disambiguationData":[OSD([sQuery(id+"F3.wireOp",EDGE,"E53.top")])]})]});
            var Q70;
            Q70=makeQuery(id+"F4.boolean.opBoolean","COPY",FACE,{"disambiguationData":[OD(1.0)],"derivedFrom":makeQuery(id+"F4.opRevolve","SWEPT_FACE",FACE,{"disambiguationData":[OSD([sQuery(id+"F3.wireOp",EDGE,"E53.top")])]})});
            var Q71;
            Q71=makeQuery(id+"F4.boolean.opBoolean","COPY",FACE,{"disambiguationData":[OD(2.0)],"derivedFrom":makeQuery(id+"F4.opRevolve","SWEPT_FACE",FACE,{"disambiguationData":[OSD([sQuery(id+"F3.wireOp",EDGE,"E53.top")])]})});
            var Q72;
            Q72=makeQuery(id+"F4.boolean.opBoolean","INTERSECT",EDGE,{"derivedFrom":[makeQuery(id+"F2.opExtrude","SWEPT_FACE",FACE,{"disambiguationData":[OSD([sQuery(id+"F1.wireOp",EDGE,"E20.2.4"),sQuery(id+"F1.wireOp",EDGE,"E20.2.5")])]}),makeQuery(id+"F4.opRevolve","SWEPT_FACE",FACE,{"disambiguationData":[OSD([sQuery(id+"F3.wireOp",EDGE,"E53.bottom")])]})]});
            var Q73;
            Q73=makeQuery(id+"F4.boolean.opBoolean","INTERSECT",EDGE,{"derivedFrom":[makeQuery(id+"F2.opExtrude","SWEPT_FACE",FACE,{"disambiguationData":[OSD([sQuery(id+"F1.wireOp",EDGE,"E20.1.4"),sQuery(id+"F1.wireOp",EDGE,"E20.1.5")])]}),makeQuery(id+"F4.opRevolve","SWEPT_FACE",FACE,{"disambiguationData":[OSD([sQuery(id+"F3.wireOp",EDGE,"E53.bottom")])]})]});
            var Q74;
            Q74=makeQuery(id+"F4.boolean.opBoolean","INTERSECT",EDGE,{"derivedFrom":[makeQuery(id+"F2.opExtrude","SWEPT_FACE",FACE,{"disambiguationData":[OSD([sQuery(id+"F1.wireOp",EDGE,"E21.14.3.0"),sQuery(id+"F1.wireOp",EDGE,"E21.18.3.0")])]}),makeQuery(id+"F4.opRevolve","SWEPT_FACE",FACE,{"disambiguationData":[OSD([sQuery(id+"F3.wireOp",EDGE,"E53.top")])]})]});
            var Q75;
            Q75=makeQuery(id+"F4.boolean.opBoolean","INTERSECT",EDGE,{"derivedFrom":[makeQuery(id+"F2.opExtrude","SWEPT_FACE",FACE,{"disambiguationData":[OSD([sQuery(id+"F1.wireOp",EDGE,"E21.14.3.0"),sQuery(id+"F1.wireOp",EDGE,"E21.18.3.0")])]}),makeQuery(id+"F4.opRevolve","SWEPT_FACE",FACE,{"disambiguationData":[OSD([sQuery(id+"F3.wireOp",EDGE,"E53.bottom")])]})]});
            var Q76;
            Q76=makeQuery(id+"F4.boolean.opBoolean","INTERSECT",EDGE,{"derivedFrom":[makeQuery(id+"F2.opExtrude","SWEPT_FACE",FACE,{"disambiguationData":[OSD([sQuery(id+"F1.wireOp",EDGE,"E22.26.17.0")])]}),makeQuery(id+"F4.opRevolve","SWEPT_FACE",FACE,{"disambiguationData":[OSD([sQuery(id+"F3.wireOp",EDGE,"E53.top")])]})]});
            var Q77;
            Q77=makeQuery(id+"F4.boolean.opBoolean","INTERSECT",EDGE,{"derivedFrom":[makeQuery(id+"F2.opExtrude","SWEPT_FACE",FACE,{"disambiguationData":[OSD([sQuery(id+"F1.wireOp",EDGE,"E22.26.17.0")])]}),makeQuery(id+"F4.opRevolve","SWEPT_FACE",FACE,{"disambiguationData":[OSD([sQuery(id+"F3.wireOp",EDGE,"E53.bottom")])]})]});
            var Q78;
            Q78=makeQuery(id+"F4.boolean.opBoolean","INTERSECT",EDGE,{"derivedFrom":[makeQuery(id+"F2.opExtrude","SWEPT_FACE",FACE,{"disambiguationData":[OSD([sQuery(id+"F1.wireOp",EDGE,"E22.26.18.0")])]}),makeQuery(id+"F4.opRevolve","SWEPT_FACE",FACE,{"disambiguationData":[OSD([sQuery(id+"F3.wireOp",EDGE,"E53.bottom")])]})]});
            var Q79;
            Q79=makeQuery(id+"F4.boolean.opBoolean","INTERSECT",EDGE,{"derivedFrom":[makeQuery(id+"F2.opExtrude","SWEPT_FACE",FACE,{"disambiguationData":[OSD([sQuery(id+"F1.wireOp",EDGE,"E22.26.18.0")])]}),makeQuery(id+"F4.opRevolve","SWEPT_FACE",FACE,{"disambiguationData":[OSD([sQuery(id+"F3.wireOp",EDGE,"E53.top")])]})]});
            var Q80;
            Q80=makeQuery(id+"F4.boolean.opBoolean","INTERSECT",EDGE,{"derivedFrom":[makeQuery(id+"F2.opExtrude","SWEPT_FACE",FACE,{"disambiguationData":[OSD([sQuery(id+"F1.wireOp",EDGE,"E22.14.17.0"),sQuery(id+"F1.wireOp",EDGE,"E22.18.17.0")])]}),makeQuery(id+"F4.opRevolve","SWEPT_FACE",FACE,{"disambiguationData":[OSD([sQuery(id+"F3.wireOp",EDGE,"E53.top")])]})]});
            var Q81;
            Q81=makeQuery(id+"F4.boolean.opBoolean","INTERSECT",EDGE,{"derivedFrom":[makeQuery(id+"F2.opExtrude","SWEPT_FACE",FACE,{"disambiguationData":[OSD([sQuery(id+"F1.wireOp",EDGE,"E22.14.17.0"),sQuery(id+"F1.wireOp",EDGE,"E22.18.17.0")])]}),makeQuery(id+"F4.opRevolve","SWEPT_FACE",FACE,{"disambiguationData":[OSD([sQuery(id+"F3.wireOp",EDGE,"E53.bottom")])]})]});
            var Q82;
            Q82=makeQuery(id+"F4.boolean.opBoolean","INTERSECT",EDGE,{"derivedFrom":[makeQuery(id+"F2.opExtrude","SWEPT_FACE",FACE,{"disambiguationData":[OSD([sQuery(id+"F1.wireOp",EDGE,"E22.14.18.0"),sQuery(id+"F1.wireOp",EDGE,"E22.18.18.0")])]}),makeQuery(id+"F4.opRevolve","SWEPT_FACE",FACE,{"disambiguationData":[OSD([sQuery(id+"F3.wireOp",EDGE,"E53.bottom")])]})]});
            var Q83;
            Q83=makeQuery(id+"F4.boolean.opBoolean","COPY",FACE,{"disambiguationData":[OD(18.0)],"derivedFrom":makeQuery(id+"F4.opRevolve","SWEPT_FACE",FACE,{"disambiguationData":[OSD([sQuery(id+"F3.wireOp",EDGE,"E53.top")])]})});
            var Q84;
            Q84=makeQuery(id+"F4.boolean.opBoolean","COPY",FACE,{"disambiguationData":[OD(16.0)],"derivedFrom":makeQuery(id+"F4.opRevolve","SWEPT_FACE",FACE,{"disambiguationData":[OSD([sQuery(id+"F3.wireOp",EDGE,"E53.top")])]})});
            var Q85;
            Q85=makeQuery(id+"F4.boolean.opBoolean","COPY",FACE,{"disambiguationData":[OD(15.0)],"derivedFrom":makeQuery(id+"F4.opRevolve","SWEPT_FACE",FACE,{"disambiguationData":[OSD([sQuery(id+"F3.wireOp",EDGE,"E53.top")])]})});
            var Q86;
            Q86=makeQuery(id+"F4.boolean.opBoolean","COPY",FACE,{"disambiguationData":[OD(14.0)],"derivedFrom":makeQuery(id+"F4.opRevolve","SWEPT_FACE",FACE,{"disambiguationData":[OSD([sQuery(id+"F3.wireOp",EDGE,"E53.top")])]})});
            var Q87;
            Q87=makeQuery(id+"F4.boolean.opBoolean","COPY",FACE,{"disambiguationData":[OD(19.0)],"derivedFrom":makeQuery(id+"F4.opRevolve","SWEPT_FACE",FACE,{"disambiguationData":[OSD([sQuery(id+"F3.wireOp",EDGE,"E53.top")])]})});
            var Q88;
            Q88=makeQuery(id+"F4.boolean.opBoolean","COPY",FACE,{"disambiguationData":[OD(19.0)],"derivedFrom":makeQuery(id+"F4.opRevolve","SWEPT_FACE",FACE,{"disambiguationData":[OSD([sQuery(id+"F3.wireOp",EDGE,"E53.bottom")])]})});
            var Q89;
            Q89=makeQuery(id+"F4.boolean.opBoolean","COPY",FACE,{"disambiguationData":[OD(4.0)],"derivedFrom":makeQuery(id+"F4.opRevolve","SWEPT_FACE",FACE,{"disambiguationData":[OSD([sQuery(id+"F3.wireOp",EDGE,"E53.top")])]})});
            var Q90;
            Q90=makeQuery(id+"F4.boolean.opBoolean","COPY",FACE,{"disambiguationData":[OD(5.0)],"derivedFrom":makeQuery(id+"F4.opRevolve","SWEPT_FACE",FACE,{"disambiguationData":[OSD([sQuery(id+"F3.wireOp",EDGE,"E53.top")])]})});
            var Q91;
            Q91=makeQuery(id+"F4.boolean.opBoolean","COPY",FACE,{"disambiguationData":[OD(6.0)],"derivedFrom":makeQuery(id+"F4.opRevolve","SWEPT_FACE",FACE,{"disambiguationData":[OSD([sQuery(id+"F3.wireOp",EDGE,"E53.top")])]})});
            var Q92;
            Q92=makeQuery(id+"F4.boolean.opBoolean","COPY",FACE,{"disambiguationData":[OD(7.0)],"derivedFrom":makeQuery(id+"F4.opRevolve","SWEPT_FACE",FACE,{"disambiguationData":[OSD([sQuery(id+"F3.wireOp",EDGE,"E53.top")])]})});
            var Q93;
            Q93=makeQuery(id+"F4.boolean.opBoolean","COPY",FACE,{"disambiguationData":[OD(8.0)],"derivedFrom":makeQuery(id+"F4.opRevolve","SWEPT_FACE",FACE,{"disambiguationData":[OSD([sQuery(id+"F3.wireOp",EDGE,"E53.top")])]})});
            var Q94;
            Q94=makeQuery(id+"F4.boolean.opBoolean","COPY",FACE,{"disambiguationData":[OD(9.0)],"derivedFrom":makeQuery(id+"F4.opRevolve","SWEPT_FACE",FACE,{"disambiguationData":[OSD([sQuery(id+"F3.wireOp",EDGE,"E53.top")])]})});
            var Q95;
            Q95=makeQuery(id+"F4.boolean.opBoolean","COPY",FACE,{"disambiguationData":[OD(10.0)],"derivedFrom":makeQuery(id+"F4.opRevolve","SWEPT_FACE",FACE,{"disambiguationData":[OSD([sQuery(id+"F3.wireOp",EDGE,"E53.top")])]})});
            var Q96;
            Q96=makeQuery(id+"F4.boolean.opBoolean","COPY",FACE,{"disambiguationData":[OD(11.0)],"derivedFrom":makeQuery(id+"F4.opRevolve","SWEPT_FACE",FACE,{"disambiguationData":[OSD([sQuery(id+"F3.wireOp",EDGE,"E53.top")])]})});
            var Q97;
            Q97=makeQuery(id+"F4.boolean.opBoolean","COPY",FACE,{"disambiguationData":[OD(12.0)],"derivedFrom":makeQuery(id+"F4.opRevolve","SWEPT_FACE",FACE,{"disambiguationData":[OSD([sQuery(id+"F3.wireOp",EDGE,"E53.top")])]})});
            var Q98;
            Q98=makeQuery(id+"F4.boolean.opBoolean","COPY",FACE,{"disambiguationData":[OD(13.0)],"derivedFrom":makeQuery(id+"F4.opRevolve","SWEPT_FACE",FACE,{"disambiguationData":[OSD([sQuery(id+"F3.wireOp",EDGE,"E53.top")])]})});
            var Q99;
            Q99=makeQuery(id+"F4.boolean.opBoolean","COPY",FACE,{"disambiguationData":[OD(13.0)],"derivedFrom":makeQuery(id+"F4.opRevolve","SWEPT_FACE",FACE,{"disambiguationData":[OSD([sQuery(id+"F3.wireOp",EDGE,"E53.bottom")])]})});
            var Q100;
            Q100=makeQuery(id+"F4.boolean.opBoolean","COPY",FACE,{"disambiguationData":[OD(14.0)],"derivedFrom":makeQuery(id+"F4.opRevolve","SWEPT_FACE",FACE,{"disambiguationData":[OSD([sQuery(id+"F3.wireOp",EDGE,"E53.bottom")])]})});
            var Q101;
            Q101=makeQuery(id+"F4.boolean.opBoolean","COPY",FACE,{"disambiguationData":[OD(15.0)],"derivedFrom":makeQuery(id+"F4.opRevolve","SWEPT_FACE",FACE,{"disambiguationData":[OSD([sQuery(id+"F3.wireOp",EDGE,"E53.bottom")])]})});
            var Q102;
            Q102=makeQuery(id+"F4.boolean.opBoolean","COPY",FACE,{"disambiguationData":[OD(16.0)],"derivedFrom":makeQuery(id+"F4.opRevolve","SWEPT_FACE",FACE,{"disambiguationData":[OSD([sQuery(id+"F3.wireOp",EDGE,"E53.bottom")])]})});
            var Q103;
            Q103=makeQuery(id+"F4.boolean.opBoolean","COPY",FACE,{"disambiguationData":[OD(11.0)],"derivedFrom":makeQuery(id+"F4.opRevolve","SWEPT_FACE",FACE,{"disambiguationData":[OSD([sQuery(id+"F3.wireOp",EDGE,"E53.bottom")])]})});
            var Q104;
            Q104=makeQuery(id+"F4.boolean.opBoolean","COPY",FACE,{"disambiguationData":[OD(12.0)],"derivedFrom":makeQuery(id+"F4.opRevolve","SWEPT_FACE",FACE,{"disambiguationData":[OSD([sQuery(id+"F3.wireOp",EDGE,"E53.bottom")])]})});
            var Q105;
            Q105=makeQuery(id+"F4.boolean.opBoolean","COPY",FACE,{"disambiguationData":[OD(9.0)],"derivedFrom":makeQuery(id+"F4.opRevolve","SWEPT_FACE",FACE,{"disambiguationData":[OSD([sQuery(id+"F3.wireOp",EDGE,"E53.bottom")])]})});
            var Q106;
            Q106=makeQuery(id+"F4.boolean.opBoolean","COPY",FACE,{"disambiguationData":[OD(10.0)],"derivedFrom":makeQuery(id+"F4.opRevolve","SWEPT_FACE",FACE,{"disambiguationData":[OSD([sQuery(id+"F3.wireOp",EDGE,"E53.bottom")])]})});
            var Q107;
            Q107=makeQuery(id+"F4.boolean.opBoolean","COPY",FACE,{"disambiguationData":[OD(8.0)],"derivedFrom":makeQuery(id+"F4.opRevolve","SWEPT_FACE",FACE,{"disambiguationData":[OSD([sQuery(id+"F3.wireOp",EDGE,"E53.bottom")])]})});
            var Q108;
            Q108=makeQuery(id+"F4.boolean.opBoolean","COPY",FACE,{"disambiguationData":[OD(7.0)],"derivedFrom":makeQuery(id+"F4.opRevolve","SWEPT_FACE",FACE,{"disambiguationData":[OSD([sQuery(id+"F3.wireOp",EDGE,"E53.bottom")])]})});
            var Q109;
            Q109=makeQuery(id+"F4.boolean.opBoolean","COPY",FACE,{"disambiguationData":[OD(6.0)],"derivedFrom":makeQuery(id+"F4.opRevolve","SWEPT_FACE",FACE,{"disambiguationData":[OSD([sQuery(id+"F3.wireOp",EDGE,"E53.bottom")])]})});
            var Q110;
            Q110=makeQuery(id+"F4.boolean.opBoolean","COPY",FACE,{"disambiguationData":[OD(5.0)],"derivedFrom":makeQuery(id+"F4.opRevolve","SWEPT_FACE",FACE,{"disambiguationData":[OSD([sQuery(id+"F3.wireOp",EDGE,"E53.bottom")])]})});
            var Q111;
            Q111=makeQuery(id+"F4.boolean.opBoolean","COPY",FACE,{"disambiguationData":[OD(4.0)],"derivedFrom":makeQuery(id+"F4.opRevolve","SWEPT_FACE",FACE,{"disambiguationData":[OSD([sQuery(id+"F3.wireOp",EDGE,"E53.bottom")])]})});
            var Q112;
            Q112=makeQuery(id+"F4.boolean.opBoolean","COPY",FACE,{"disambiguationData":[OD(3.0)],"derivedFrom":makeQuery(id+"F4.opRevolve","SWEPT_FACE",FACE,{"disambiguationData":[OSD([sQuery(id+"F3.wireOp",EDGE,"E53.bottom")])]})});
            chamfer(context, id + "F9", {"entities" : qUnion([Q0, Q1, Q2, Q3, Q4, Q5, Q6, Q7, Q8, Q9, Q10, Q11, Q12, Q13, Q14, Q15, Q16, Q17, Q18, Q19, Q20, Q21, Q22, Q23, Q24, Q25, Q26, Q27, Q28, Q29, Q30, Q31, Q32, Q33, Q34, Q35, Q36, Q37, Q38, Q39, Q40, Q41, Q42, Q43, Q44, Q45, Q46, Q47, Q48, Q49, Q50, Q51, Q52, Q53, Q54, Q55, Q56, Q57, Q58, Q59, Q60, Q61, Q62, Q63, Q64, Q65, Q66, Q67, Q68, Q69, Q70, Q71, Q72, Q73, Q74, Q75, Q76, Q77, Q78, Q79, Q80, Q81, Q82, Q83, Q84, Q85, Q86, Q87, Q88, Q89, Q90, Q91, Q92, Q93, Q94, Q95, Q96, Q97, Q98, Q99, Q100, Q101, Q102, Q103, Q104, Q105, Q106, Q107, Q108, Q109, Q110, Q111, Q112]), "chamferType" : ChamferType.OFFSET_ANGLE, "width" : 2.5 * mm, "oppositeDirection" : false, "angle" : 45 * degree, "tangentPropagation" : true});
        }
    });
